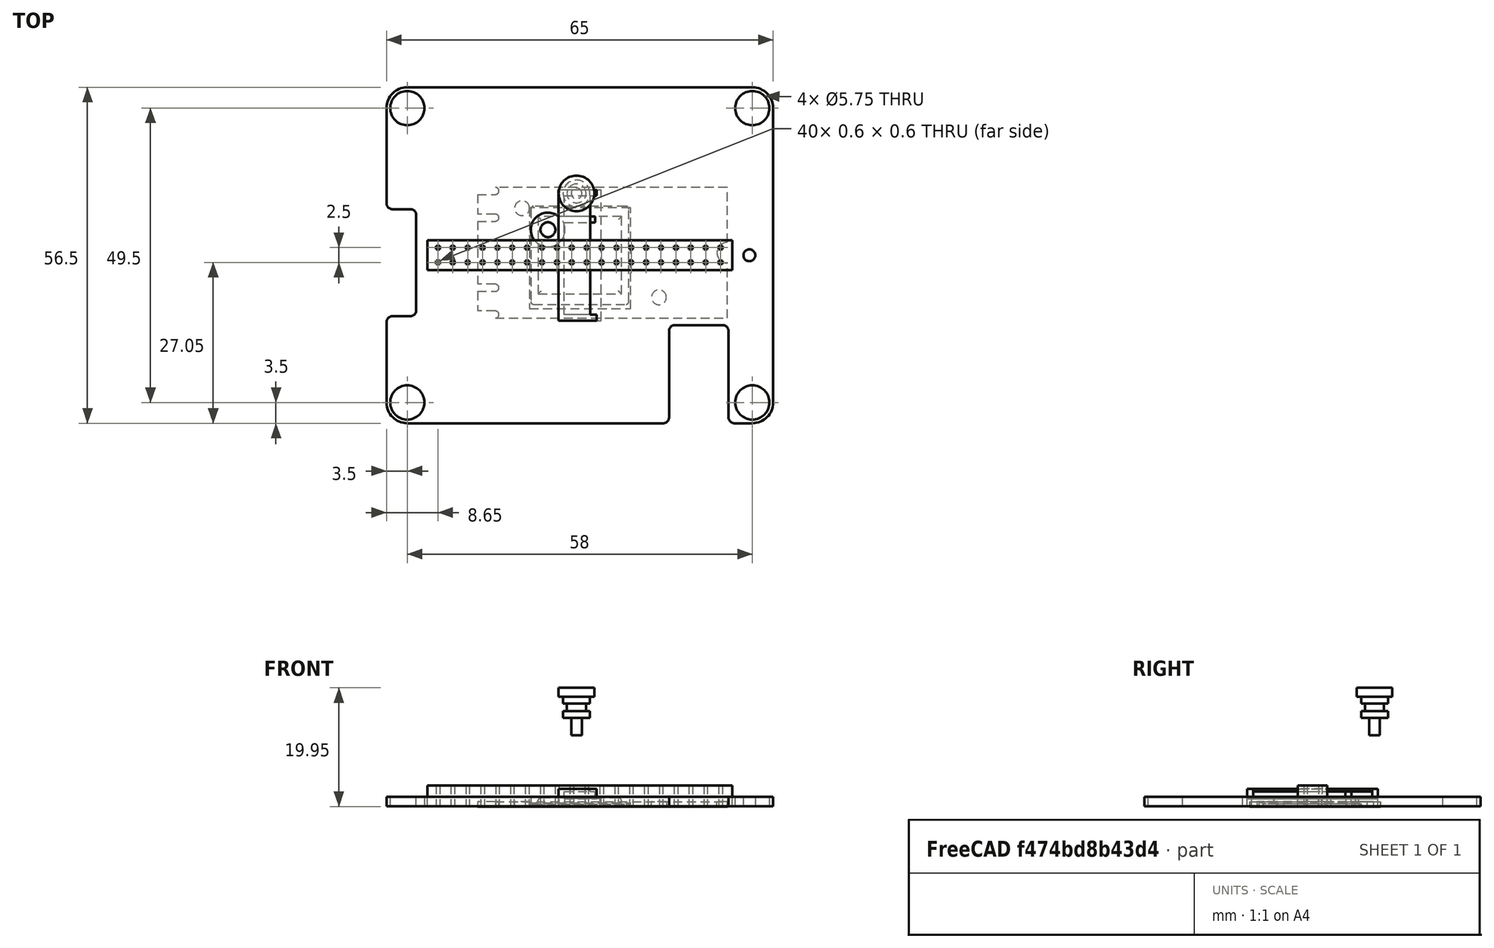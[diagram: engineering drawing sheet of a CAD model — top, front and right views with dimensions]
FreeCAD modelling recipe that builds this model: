
FCSTD DOCUMENT  (FreeCAD 1.0R39109 (Git))
Label: Raspberry Pi AI Kit
License: All rights reserved
LicenseURL: https://en.wikipedia.org/wiki/All_rights_reserved
objects: App::Link×21, Sketcher::SketchObject×14, App::FeaturePython×14, PartDesign::Pad×10, PartDesign::Body×8, PartDesign::Pocket×3, Assembly::JointGroup×3, Assembly::AssemblyObject×3, App::Part×2, Assembly::AssemblyLink×2, PartDesign::Revolution×1, PartDesign::Fillet×1
note: 81 computed .brp shape members not serialized (recipe doc carries the construction recipe); baked Part::Feature solids carry a one-line shape summary decoded from their .brp

FEATURE [Sketcher::SketchObject] Sketch
  ArcFitTolerance = 1e-06
  AttachmentSupport = -> [XY_Plane003]
  FullyConstrained = true
  MakeInternals = false
  MapMode = 5
  sketch-geometry (6):
    g0: LineSegment StartX=-21 StartY=11 StartZ=0 EndX=-21 EndY=-11 EndZ=0
    g1: LineSegment StartX=-21 StartY=-11 StartZ=0 EndX=21 EndY=-11 EndZ=0
    g2: LineSegment StartX=21 StartY=-11 StartZ=0 EndX=21 EndY=11 EndZ=0
    g3: LineSegment StartX=21 StartY=11 StartZ=0 EndX=-21 EndY=11 EndZ=0
    g4: GeomPoint X=0 Y=11 Z=0
    g5: GeomPoint X=-21 Y=0 Z=0
  constraints (14):
    c: Coincident(g0,g1)
    c: Coincident(g1,g2)
    c: Coincident(g2,g3)
    c: Coincident(g3,g0)
    c: Vertical(g0)
    c: Vertical(g2)
    c: Horizontal(g1)
    c: Horizontal(g3)
    c: DistanceY(g2,g2) = 22
    c: DistanceX(g3,g3) = 42
    c: Symmetric(g3,g3,g4)
    c: Symmetric(g0,g0,g5)
    c: Vertical(g4,g-1)
    c: Horizontal(g5,g-1)
FEATURE [PartDesign::Pad] Pad
  Direction = (0,0,1)
  Length = 0.8
  Length2 = 10
  Profile = -> Sketch
  ReferenceAxis = -> Sketch [N_Axis]
  Refine = true
  Suppressed = false
  Type = 0
FEATURE [Sketcher::SketchObject] Sketch001
  ArcFitTolerance = 1e-06
  AttachmentSupport = -> [Pad]
  ExternalGeometry = -> [Pad]
  FullyConstrained = true
  MakeInternals = false
  MapMode = 5
  Placement = pos=(0,0,0.8) rot=(0,0,1;0rad)
  sketch-geometry (27):
    g0: LineSegment StartX=-21 StartY=-9.8 StartZ=0 EndX=-21 EndY=-11 EndZ=0
    g1: LineSegment StartX=-21 StartY=-11 StartZ=0 EndX=-18 EndY=-11 EndZ=0
    g2: LineSegment StartX=-18 StartY=-11 StartZ=0 EndX=-18 EndY=-9.8 EndZ=0
    g3: LineSegment StartX=-18 StartY=-9.8 StartZ=0 EndX=-21 EndY=-9.8 EndZ=0
    g4: GeomPoint X=-18 Y=-10.4 Z=0
    g5: Circle CenterX=-18 CenterY=-10.4 CenterZ=0 NormalX=0 NormalY=0 NormalZ=1 AngleXU=0 Radius=0.6
    g6: Circle CenterX=21 CenterY=0 CenterZ=0 NormalX=0 NormalY=0 NormalZ=1 AngleXU=0 Radius=1.75
    g7: LineSegment StartX=-21 StartY=11 StartZ=0 EndX=-21 EndY=9.8 EndZ=0
    g8: LineSegment StartX=-21 StartY=9.8 StartZ=0 EndX=-18 EndY=9.8 EndZ=0
    g9: LineSegment StartX=-18 StartY=9.8 StartZ=0 EndX=-18 EndY=11 EndZ=0
    g10: LineSegment StartX=-18 StartY=11 StartZ=0 EndX=-21 EndY=11 EndZ=0
    g11: GeomPoint X=-18 Y=10.4 Z=0
    g12: Circle CenterX=-18 CenterY=10.4 CenterZ=0 NormalX=0 NormalY=0 NormalZ=1 AngleXU=0 Radius=0.6
    g13: LineSegment StartX=-21 StartY=6.5 StartZ=0 EndX=-21 EndY=5.3 EndZ=0
    g14: LineSegment StartX=-21 StartY=5.3 StartZ=0 EndX=-18 EndY=5.3 EndZ=0
    g15: LineSegment StartX=-18 StartY=5.3 StartZ=0 EndX=-18 EndY=6.5 EndZ=0
    g16: LineSegment StartX=-18 StartY=6.5 StartZ=0 EndX=-21 EndY=6.5 EndZ=0
    g17: GeomPoint X=-18 Y=5.9 Z=0
    g18: Circle CenterX=-18 CenterY=5.9 CenterZ=0 NormalX=0 NormalY=0 NormalZ=1 AngleXU=0 Radius=0.6
    g19: LineSegment StartX=-21 StartY=-5.3 StartZ=0 EndX=-21 EndY=-6.5 EndZ=0
    g20: LineSegment StartX=-21 StartY=-6.5 StartZ=0 EndX=-18 EndY=-6.5 EndZ=0
    g21: LineSegment StartX=-18 StartY=-6.5 StartZ=0 EndX=-18 EndY=-5.3 EndZ=0
    g22: LineSegment StartX=-18 StartY=-5.3 StartZ=0 EndX=-21 EndY=-5.3 EndZ=0
    g23: GeomPoint X=-18 Y=-5.9 Z=0
    g24: Circle CenterX=-18 CenterY=-5.9 CenterZ=0 NormalX=0 NormalY=0 NormalZ=1 AngleXU=0 Radius=0.6
    g25: Circle CenterX=-13.5 CenterY=7.5 CenterZ=0 NormalX=0 NormalY=0 NormalZ=1 AngleXU=0 Radius=1.25
    g26: Circle CenterX=9.5 CenterY=-7.5 CenterZ=0 NormalX=0 NormalY=0 NormalZ=1 AngleXU=0 Radius=1.25
  constraints (66):
    c: Coincident(g0,g1)
    c: Coincident(g1,g2)
    c: Coincident(g2,g3)
    c: Coincident(g3,g0)
    c: Vertical(g0)
    c: Vertical(g2)
    c: Horizontal(g1)
    c: Horizontal(g3)
    c: Symmetric(g2,g2,g4)
    c: Coincident(g5,g4)
    c: PointOnObject(g2,g5)
    c: Distance(g1,g3) = 1.2
    c: DistanceX(g3,g3) = 3
    c: Symmetric(g-6,g-6,g6)
    c: Diameter(g6) = 3.5
    c: Coincident(g7,g8)
    c: Coincident(g8,g9)
    c: Coincident(g9,g10)
    c: Coincident(g10,g7)
    c: Vertical(g7)
    c: Vertical(g9)
    c: Horizontal(g8)
    c: Horizontal(g10)
    c: Symmetric(g9,g9,g11)
    c: Coincident(g12,g11)
    c: PointOnObject(g9,g12)
    c: Distance(g8,g10) = 1.2
    c: DistanceX(g10,g10) = 3
    c: Coincident(g0,g-5)
    c: Coincident(g13,g14)
    c: Coincident(g14,g15)
    c: Coincident(g15,g16)
    c: Coincident(g16,g13)
    c: Vertical(g13)
    c: Vertical(g15)
    c: Horizontal(g14)
    c: Horizontal(g16)
    c: Symmetric(g15,g15,g17)
    c: Coincident(g18,g17)
    c: PointOnObject(g15,g18)
    c: Distance(g14,g16) = 1.2
    c: DistanceX(g16,g16) = 3
    c: Coincident(g19,g20)
    c: Coincident(g20,g21)
    c: Coincident(g21,g22)
    c: Coincident(g22,g19)
    c: Vertical(g19)
    c: Vertical(g21)
    c: Horizontal(g20)
    c: Horizontal(g22)
    c: Symmetric(g21,g21,g23)
    c: Coincident(g24,g23)
    c: PointOnObject(g21,g24)
    c: Distance(g20,g22) = 1.2
    c: DistanceX(g22,g22) = 3
    c: Coincident(g7,g-4)
    c: Distance(g-4,g16) = 4.5
    c: PointOnObject(g13,g-3)
    c: Distance(g-5,g20) = 4.5
    c: PointOnObject(g19,g-3)
    c: Diameter(g25) = 2.5
    c: Diameter(g26) = 2.5
    c: Distance(g25,g-5) = 18.5
    c: Distance(g25,g-3) = 7.5
    c: Distance(g26,g-5) = 3.5
    c: Distance(g26,g-3) = 30.5
FEATURE [PartDesign::Pocket] Pocket
  BaseFeature = -> Pad
  Direction = (0,0,-1)
  Length = 5
  Length2 = 5
  Profile = -> Sketch001
  ReferenceAxis = -> Sketch001 [N_Axis]
  Refine = true
  Suppressed = false
  Type = 0
FEATURE [PartDesign::Body] Body  label="Board"
  AllowCompound = false
  Group = -> [Sketch,Pad,Sketch001,Pocket]
  Origin = -> Origin003
  Placement = pos=(3.79899,0.428775,-0.0438795) rot=(0,0,1;0rad)
  Tip = -> Pocket
FEATURE [Sketcher::SketchObject] Sketch002
  ArcFitTolerance = 1e-06
  AttachmentSupport = -> [XZ_Plane004]
  FullyConstrained = false
  MakeInternals = false
  MapMode = 5
  Placement = pos=(0,0,0) rot=(1,0,0;1.5708rad)
  sketch-geometry (20):
    g0: LineSegment StartX=0 StartY=8.4139 StartZ=0 EndX=-0.9 EndY=8.4139 EndZ=0
    g1: LineSegment StartX=-0.9 StartY=8.4139 StartZ=0 EndX=-0.9 EndY=0.413896 EndZ=0
    g2: LineSegment StartX=-0.9 StartY=0.413896 StartZ=0 EndX=0 EndY=0.413896 EndZ=0
    g3: LineSegment StartX=0 StartY=0.413896 StartZ=0 EndX=0 EndY=8.4139 EndZ=0
    g4: LineSegment StartX=-0.9 StartY=8.4139 StartZ=0 EndX=-3 EndY=8.4139 EndZ=0
    g5: LineSegment StartX=-3 StartY=8.4139 StartZ=0 EndX=-3 EndY=6.9139 EndZ=0
    g6: LineSegment StartX=-3 StartY=6.9139 StartZ=0 EndX=-0.9 EndY=6.9139 EndZ=0
    g7: LineSegment StartX=-0.9 StartY=6.9139 StartZ=0 EndX=-0.9 EndY=8.4139 EndZ=0
    g8: LineSegment StartX=-2.25 StartY=6.9139 StartZ=0 EndX=-2.25 EndY=5.7639 EndZ=0
    g9: LineSegment StartX=-2.25 StartY=5.7639 StartZ=0 EndX=-0.9 EndY=5.7639 EndZ=0
    g10: LineSegment StartX=-0.9 StartY=5.7639 StartZ=0 EndX=-0.9 EndY=6.9139 EndZ=0
    g11: LineSegment StartX=-0.9 StartY=6.9139 StartZ=0 EndX=-2.25 EndY=6.9139 EndZ=0
    g12: LineSegment StartX=-0.9 StartY=4.5139 StartZ=0 EndX=-2.25 EndY=4.5139 EndZ=0
    g13: LineSegment StartX=-2.25 StartY=4.5139 StartZ=0 EndX=-2.25 EndY=3.3639 EndZ=0
    g14: LineSegment StartX=-2.25 StartY=3.3639 StartZ=0 EndX=-0.9 EndY=3.3639 EndZ=0
    g15: LineSegment StartX=-0.9 StartY=3.3639 StartZ=0 EndX=-0.9 EndY=4.5139 EndZ=0
    g16: LineSegment StartX=-1.6 StartY=5.7639 StartZ=0 EndX=-1.6 EndY=4.5139 EndZ=0
    g17: LineSegment StartX=-1.6 StartY=4.5139 StartZ=0 EndX=-0.9 EndY=4.5139 EndZ=0
    g18: LineSegment StartX=-0.9 StartY=4.5139 StartZ=0 EndX=-0.9 EndY=5.7639 EndZ=0
    g19: LineSegment StartX=-0.9 StartY=5.7639 StartZ=0 EndX=-1.6 EndY=5.7639 EndZ=0
  constraints (57):
    c: Coincident(g0,g1)
    c: Coincident(g1,g2)
    c: Coincident(g2,g3)
    c: Coincident(g3,g0)
    c: Horizontal(g0)
    c: Horizontal(g2)
    c: Vertical(g1)
    c: Vertical(g3)
    c: PointOnObject(g0,g-2)
    c: DistanceX(g0,g0) = 0.9
    c: Coincident(g4,g5)
    c: Coincident(g5,g6)
    c: Coincident(g6,g7)
    c: Coincident(g7,g4)
    c: Horizontal(g4)
    c: Horizontal(g6)
    c: Vertical(g5)
    c: Vertical(g7)
    c: Coincident(g4,g0)
    c: DistanceY(g3,g3) = 8
    c: Distance(g6,g4) = 1.5
    c: DistanceX(g4,g0) = 3
    c: Coincident(g8,g9)
    c: Coincident(g9,g10)
    c: Coincident(g10,g11)
    c: Coincident(g11,g8)
    c: Vertical(g8)
    c: Vertical(g10)
    c: Horizontal(g9)
    c: Horizontal(g11)
    c: PointOnObject(g8,g6)
    c: PointOnObject(g9,g1)
    c: Distance(g8,g3) = 2.25
    c: DistanceY(g8,g8) = 1.15
    c: Coincident(g12,g13)
    c: Coincident(g13,g14)
    c: Coincident(g14,g15)
    c: Coincident(g15,g12)
    c: Horizontal(g12)
    c: Horizontal(g14)
    c: Vertical(g13)
    c: Vertical(g15)
    c: PointOnObject(g12,g1)
    c: DistanceY(g13,g13) = 1.15
    c: Distance(g12,g9) = 1.25
    c: Vertical(g8,g12)
    c: Coincident(g16,g17)
    c: Coincident(g17,g18)
    c: Coincident(g18,g19)
    c: Coincident(g19,g16)
    c: Vertical(g16)
    c: Vertical(g18)
    c: Horizontal(g17)
    c: Horizontal(g19)
    c: PointOnObject(g16,g9)
    c: Coincident(g17,g12)
    c: Distance(g3,g16) = 1.6
FEATURE [PartDesign::Revolution] Revolution
  Angle = 360
  Angle2 = 60
  Axis = (0,2e-16,1)
  Base = (0,0,0)
  Placement = pos=(0,0,0) rot=(1,0,0;1.5708rad)
  Profile = -> Sketch002
  ReferenceAxis = -> Sketch002 [V_Axis]
  Refine = true
  Suppressed = false
  Type = 0
FEATURE [PartDesign::Body] Body001  label="Pin"
  AllowCompound = false
  Group = -> [Sketch002,Revolution]
  Origin = -> Origin004
  Placement = pos=(-0.558638,10.4085,11.496) rot=(0,0,1;0rad)
  Tip = -> Revolution
FEATURE [Sketcher::SketchObject] Sketch003
  ArcFitTolerance = 1e-06
  AttachmentSupport = -> [XY_Plane007]
  FullyConstrained = false
  MakeInternals = false
  MapMode = 5
  sketch-geometry (4):
    g0: LineSegment StartX=-8.47777 StartY=8.01213 StartZ=0 EndX=-8.47777 EndY=-8.98787 EndZ=0
    g1: LineSegment StartX=-8.47777 StartY=-8.98787 StartZ=0 EndX=8.52223 EndY=-8.98787 EndZ=0
    g2: LineSegment StartX=8.52223 StartY=-8.98787 StartZ=0 EndX=8.52223 EndY=8.01213 EndZ=0
    g3: LineSegment StartX=8.52223 StartY=8.01213 StartZ=0 EndX=-8.47777 EndY=8.01213 EndZ=0
  constraints (10):
    c: Coincident(g0,g1)
    c: Coincident(g1,g2)
    c: Coincident(g2,g3)
    c: Coincident(g3,g0)
    c: Vertical(g0)
    c: Vertical(g2)
    c: Horizontal(g1)
    c: Horizontal(g3)
    c: DistanceX(g3,g3) = 17
    c: DistanceY(g2,g2) = 17
FEATURE [PartDesign::Pad] Pad001
  Direction = (0,0,1)
  Length = 0.6
  Length2 = 10
  Profile = -> Sketch003
  ReferenceAxis = -> Sketch003 [N_Axis]
  Refine = true
  Suppressed = false
  Type = 0
FEATURE [PartDesign::Body] Body002  label="Chip Platform"
  AllowCompound = false
  Group = -> [Sketch003,Pad001]
  Origin = -> Origin007
  Tip = -> Pad001
FEATURE [Sketcher::SketchObject] Sketch004
  ArcFitTolerance = 1e-06
  AttachmentSupport = -> [XY_Plane008]
  FullyConstrained = true
  MakeInternals = false
  MapMode = 5
  sketch-geometry (14):
    g0: LineSegment StartX=-8.25 StartY=7.75 StartZ=0 EndX=-8.25 EndY=-7.75 EndZ=0
    g1: LineSegment StartX=-7.75 StartY=-8.25 StartZ=0 EndX=7.75 EndY=-8.25 EndZ=0
    g2: LineSegment StartX=8.25 StartY=-7.75 StartZ=0 EndX=8.25 EndY=7.75 EndZ=0
    g3: LineSegment StartX=7.75 StartY=8.25 StartZ=0 EndX=-7.75 EndY=8.25 EndZ=0
    g4: GeomPoint X=8.25 Y=0 Z=0
    g5: GeomPoint X=0 Y=8.25 Z=0
    g6: ArcOfCircle CenterX=7.75 CenterY=7.75 CenterZ=0 NormalX=0 NormalY=0 NormalZ=1 AngleXU=0 Radius=0.5 StartAngle=2e-16 EndAngle=1.5708
    g7: GeomPoint [constr] X=8.25 Y=8.25 Z=0
    g8: ArcOfCircle CenterX=-7.75 CenterY=7.75 CenterZ=0 NormalX=0 NormalY=0 NormalZ=1 AngleXU=0 Radius=0.5 StartAngle=1.5708 EndAngle=3.14159
    g9: GeomPoint [constr] X=-8.25 Y=8.25 Z=0
    g10: ArcOfCircle CenterX=-7.75 CenterY=-7.75 CenterZ=0 NormalX=0 NormalY=0 NormalZ=1 AngleXU=0 Radius=0.5 StartAngle=3.14159 EndAngle=4.71239
    g11: GeomPoint [constr] X=-8.25 Y=-8.25 Z=0
    g12: ArcOfCircle CenterX=7.75 CenterY=-7.75 CenterZ=0 NormalX=0 NormalY=0 NormalZ=1 AngleXU=0 Radius=0.5 StartAngle=4.71239 EndAngle=6.28319
    g13: GeomPoint [constr] X=8.25 Y=-8.25 Z=0
  constraints (30):
    c: Vertical(g0)
    c: Vertical(g2)
    c: Horizontal(g1)
    c: Horizontal(g3)
    c: DistanceX(g9,g7) = 16.5
    c: DistanceY(g13,g7) = 16.5
    c: Symmetric(g13,g7,g4)
    c: Symmetric(g7,g9,g5)
    c: Vertical(g5,g-1)
    c: Horizontal(g4,g-1)
    c: PointOnObject(g7,g2)
    c: PointOnObject(g7,g3)
    c: Tangent(g2,g6) = -1.5708
    c: Tangent(g3,g6) = -1.5708
    c: PointOnObject(g9,g0)
    c: PointOnObject(g9,g3)
    c: Tangent(g0,g8) = -1.5708
    c: Tangent(g3,g8) = -1.5708
    c: PointOnObject(g11,g0)
    c: PointOnObject(g11,g1)
    c: Tangent(g0,g10) = -1.5708
    c: Tangent(g1,g10) = -1.5708
    c: PointOnObject(g13,g1)
    c: PointOnObject(g13,g2)
    c: Tangent(g1,g12) = -1.5708
    c: Tangent(g2,g12) = -1.5708
    c: Radius(g8) = 0.5
    c: Radius(g6) = 0.5
    c: Radius(g12) = 0.5
    c: Radius(g10) = 0.5
FEATURE [PartDesign::Pad] Pad002
  Direction = (0,0,1)
  Length = 0.4
  Length2 = 10
  Profile = -> Sketch004
  ReferenceAxis = -> Sketch004 [N_Axis]
  Refine = true
  Suppressed = false
  Type = 0
FEATURE [Sketcher::SketchObject] Sketch005
  ArcFitTolerance = 1e-06
  AttachmentSupport = -> [Pad002]
  FullyConstrained = true
  MakeInternals = false
  MapMode = 5
  Placement = pos=(0,0,0.4) rot=(0,0,1;0rad)
  sketch-geometry (6):
    g0: LineSegment StartX=-7 StartY=6.5 StartZ=0 EndX=-7 EndY=-6.5 EndZ=0
    g1: LineSegment StartX=-7 StartY=-6.5 StartZ=0 EndX=7 EndY=-6.5 EndZ=0
    g2: LineSegment StartX=7 StartY=-6.5 StartZ=0 EndX=7 EndY=6.5 EndZ=0
    g3: LineSegment StartX=7 StartY=6.5 StartZ=0 EndX=-7 EndY=6.5 EndZ=0
    g4: GeomPoint X=0 Y=6.5 Z=0
    g5: GeomPoint X=7 Y=-1e-16 Z=0
  constraints (14):
    c: Coincident(g0,g1)
    c: Coincident(g1,g2)
    c: Coincident(g2,g3)
    c: Coincident(g3,g0)
    c: Vertical(g0)
    c: Vertical(g2)
    c: Horizontal(g1)
    c: Horizontal(g3)
    c: Symmetric(g3,g3,g4)
    c: Symmetric(g2,g2,g5)
    c: Vertical(g4,g-1)
    c: Horizontal(g5,g-1)
    c: DistanceX(g3,g3) = 14
    c: DistanceY(g2,g2) = 13
FEATURE [PartDesign::Pad] Pad003
  BaseFeature = -> Pad002
  Direction = (0,0,1)
  Length = 1
  Length2 = 10
  Profile = -> Sketch005
  ReferenceAxis = -> Sketch005 [N_Axis]
  Refine = true
  Suppressed = false
  Type = 0
FEATURE [PartDesign::Fillet] Fillet
  Base = -> Pad003 [Face15]
  BaseFeature = -> Pad003
  Radius = 0.5
  Refine = true
  SupportTransform = false
  Suppressed = false
  UseAllEdges = false
FEATURE [PartDesign::Body] Body003  label="Chip"
  AllowCompound = false
  Group = -> [Sketch004,Pad002,Sketch005,Pad003,Fillet]
  Origin = -> Origin008
  Tip = -> Fillet
FEATURE [App::Part] Part  label="Hailo AI Module"
  Group = -> [Body,Body002,Body003]
  Origin = -> Origin005
  Placement = pos=(-4.7276,-1.1891,7.43734) rot=(0,0,1;0rad)
FEATURE [App::Link] Board  label="Board001"
  LinkedObject = -> Body
FEATURE [App::FeaturePython] GroundedJoint  # Assembly grounded joint (typed FeaturePython)
  ObjectToGround = -> Board
FEATURE [App::Link] Chip_Platform  label="Chip Platform001"
  LinkPlacement = pos=(-2.02223,0.487867,0.8) rot=(0,0,1;0rad)
  LinkedObject = -> Body002
  Placement = pos=(-2.02223,0.487867,0.8) rot=(0,0,1;0rad)
FEATURE [App::Link] Chip  label="Chip001"
  LinkPlacement = pos=(-2,1.8e-15,1.4) rot=(0,0,1;0rad)
  LinkedObject = -> Body003
  Placement = pos=(-2,1.8e-15,1.4) rot=(0,0,1;0rad)
FEATURE [App::FeaturePython] Joint  label="Fixed"  # Assembly joint (typed FeaturePython)
  Activated = true
  AngleMax = 0
  AngleMin = 0
  Detach1 = false
  Detach2 = false
  Distance = 0
  Distance2 = 0
  EnableAngleMax = false
  EnableAngleMin = false
  EnableLengthMax = false
  EnableLengthMin = false
  JointType = 0 (Fixed)
  LengthMax = 0
  LengthMin = 0
  Offset2 = pos=(0,-2.5,-3.5) rot=(0,0,1;0rad)
  Placement1 = pos=(0.0222293,-8.98787,0) rot=(0.707107,0,0.707107;3.14159rad)
  Placement2 = pos=(-2,-8.5,0.8) rot=(0.707107,0,0.707107;3.14159rad)
  Reference1 = -> Assembly [Chip_Platform.Edge6,Chip_Platform.Edge6]
  Reference2 = -> Assembly [Board.Edge37,Board.Edge37]
FEATURE [App::FeaturePython] Joint001  label="Fixed001"  # Assembly joint (typed FeaturePython)
  Activated = true
  AngleMax = 0
  AngleMin = 0
  Detach1 = false
  Detach2 = false
  Distance = 0
  Distance2 = 0
  EnableAngleMax = false
  EnableAngleMin = false
  EnableLengthMax = false
  EnableLengthMin = false
  JointType = 0 (Fixed)
  LengthMax = 0
  LengthMin = 0
  Offset2 = pos=(0,-0.25,0) rot=(0,0,1;0rad)
  Placement1 = pos=(0,-8.25,0) rot=(0.707107,0,0.707107;3.14159rad)
  Placement2 = pos=(0.0222293,-8.73787,0.6) rot=(0.707107,0,0.707107;3.14159rad)
  Reference1 = -> Assembly [Chip.Edge39,Chip.Edge39]
  Reference2 = -> Assembly [Chip_Platform.Edge7,Chip_Platform.Edge7]
FEATURE [Assembly::JointGroup] Joints
  Group = -> [GroundedJoint,Joint,Joint001]
FEATURE [Assembly::AssemblyObject] Assembly  label="Hailo AI Module Assembly"
  Group = -> [Joints,Board,GroundedJoint,Chip_Platform,Chip,Joint,Joint001]
  Origin = -> Origin
  Type = Assembly
FEATURE [Sketcher::SketchObject] Sketch006
  ArcFitTolerance = 1e-06
  AttachmentSupport = -> [XY_Plane010]
  FullyConstrained = true
  MakeInternals = false
  MapMode = 5
  sketch-geometry (38):
    g0: LineSegment StartX=-29 StartY=28.25 StartZ=0 EndX=29 EndY=28.25 EndZ=0
    g1: LineSegment StartX=32.5 StartY=24.75 StartZ=0 EndX=32.5 EndY=-24.75 EndZ=0
    g2: LineSegment StartX=29 StartY=-28.25 StartZ=0 EndX=26 EndY=-28.25 EndZ=0
    g3: LineSegment StartX=25 StartY=-27.25 StartZ=0 EndX=25 EndY=-12.75 EndZ=0
    g4: LineSegment StartX=24 StartY=-11.75 StartZ=0 EndX=16 EndY=-11.75 EndZ=0
    g5: LineSegment StartX=15 StartY=-12.75 StartZ=0 EndX=15 EndY=-27.25 EndZ=0
    g6: LineSegment StartX=14 StartY=-28.25 StartZ=0 EndX=-29 EndY=-28.25 EndZ=0
    g7: GeomPoint X=0 Y=28.25 Z=0
    g8: LineSegment StartX=-32.5 StartY=-24.75 StartZ=0 EndX=-32.5 EndY=-11.25 EndZ=0
    g9: LineSegment StartX=-31.5 StartY=-10.25 StartZ=0 EndX=-28.5 EndY=-10.25 EndZ=0
    g10: LineSegment StartX=-27.5 StartY=-9.25 StartZ=0 EndX=-27.5 EndY=6.75 EndZ=0
    g11: LineSegment StartX=-28.5 StartY=7.75 StartZ=0 EndX=-31.5 EndY=7.75 EndZ=0
    g12: LineSegment StartX=-32.5 StartY=8.75 StartZ=0 EndX=-32.5 EndY=24.75 EndZ=0
    g13: GeomPoint X=32.5 Y=0 Z=0
    g14: ArcOfCircle CenterX=29 CenterY=24.75 CenterZ=0 NormalX=0 NormalY=0 NormalZ=1 AngleXU=0 Radius=3.5 StartAngle=0 EndAngle=1.5708
    g15: GeomPoint [constr] X=32.5 Y=28.25 Z=0
    g16: ArcOfCircle CenterX=-29 CenterY=24.75 CenterZ=0 NormalX=0 NormalY=0 NormalZ=1 AngleXU=0 Radius=3.5 StartAngle=1.5708 EndAngle=3.14159
    g17: GeomPoint [constr] X=-32.5 Y=28.25 Z=0
    g18: ArcOfCircle CenterX=-29 CenterY=-24.75 CenterZ=0 NormalX=0 NormalY=0 NormalZ=1 AngleXU=0 Radius=3.5 StartAngle=3.14159 EndAngle=4.71239
    g19: GeomPoint [constr] X=-32.5 Y=-28.25 Z=0
    g20: ArcOfCircle CenterX=29 CenterY=-24.75 CenterZ=0 NormalX=0 NormalY=0 NormalZ=1 AngleXU=0 Radius=3.5 StartAngle=4.71239 EndAngle=6.28319
    g21: GeomPoint [constr] X=32.5 Y=-28.25 Z=0
    g22: ArcOfCircle CenterX=-31.5 CenterY=8.75 CenterZ=0 NormalX=0 NormalY=0 NormalZ=1 AngleXU=0 Radius=1 StartAngle=3.14159 EndAngle=4.71239
    g23: GeomPoint [constr] X=-32.5 Y=7.75 Z=0
    g24: ArcOfCircle CenterX=-28.5 CenterY=6.75 CenterZ=0 NormalX=0 NormalY=0 NormalZ=1 AngleXU=0 Radius=1 StartAngle=0 EndAngle=1.5708
    g25: GeomPoint [constr] X=-27.5 Y=7.75 Z=0
    g26: ArcOfCircle CenterX=-28.5 CenterY=-9.25 CenterZ=0 NormalX=0 NormalY=0 NormalZ=1 AngleXU=0 Radius=1 StartAngle=4.71239 EndAngle=6.28319
    g27: GeomPoint [constr] X=-27.5 Y=-10.25 Z=0
    g28: ArcOfCircle CenterX=-31.5 CenterY=-11.25 CenterZ=0 NormalX=0 NormalY=0 NormalZ=1 AngleXU=0 Radius=1 StartAngle=1.5708 EndAngle=3.14159
    g29: GeomPoint [constr] X=-32.5 Y=-10.25 Z=0
    g30: ArcOfCircle CenterX=14 CenterY=-27.25 CenterZ=0 NormalX=0 NormalY=0 NormalZ=1 AngleXU=0 Radius=1 StartAngle=4.71239 EndAngle=6.28319
    g31: GeomPoint [constr] X=15 Y=-28.25 Z=0
    g32: ArcOfCircle CenterX=16 CenterY=-12.75 CenterZ=0 NormalX=0 NormalY=0 NormalZ=1 AngleXU=0 Radius=1 StartAngle=1.5708 EndAngle=3.14159
    g33: GeomPoint [constr] X=15 Y=-11.75 Z=0
    g34: ArcOfCircle CenterX=24 CenterY=-12.75 CenterZ=0 NormalX=0 NormalY=0 NormalZ=1 AngleXU=0 Radius=1 StartAngle=4e-16 EndAngle=1.5708
    g35: GeomPoint [constr] X=25 Y=-11.75 Z=0
    g36: ArcOfCircle CenterX=26 CenterY=-27.25 CenterZ=0 NormalX=0 NormalY=0 NormalZ=1 AngleXU=0 Radius=1 StartAngle=3.14159 EndAngle=4.71239
    g37: GeomPoint [constr] X=25 Y=-28.25 Z=0
  constraints (86):
    c: Horizontal(g0)
    c: Vertical(g1)
    c: Horizontal(g2)
    c: Vertical(g3)
    c: Horizontal(g4)
    c: Vertical(g5)
    c: Horizontal(g6)
    c: DistanceX(g17,g15) = 65
    c: Symmetric(g17,g15,g7)
    c: Vertical(g7,g-1)
    c: Horizontal(g37,g31)
    c: DistanceX(g37,g21) = 7.5
    c: DistanceX(g33,g35) = 10
    c: DistanceY(g37,g35) = 16.5
    c: Vertical(g8)
    c: Horizontal(g9)
    c: Vertical(g10)
    c: Horizontal(g11)
    c: Vertical(g12)
    c: Vertical(g23,g29)
    c: Symmetric(g15,g21,g13)
    c: Horizontal(g13,g-1)
    c: DistanceY(g21,g15) = 56.5
    c: DistanceX(g23,g25) = 5
    c: DistanceY(g27,g25) = 18
    c: DistanceY(g19,g29) = 18
    c: PointOnObject(g15,g0)
    c: PointOnObject(g15,g1)
    c: Tangent(g0,g14) = 1.5708
    c: Tangent(g1,g14) = 1.5708
    c: PointOnObject(g17,g0)
    c: PointOnObject(g17,g12)
    c: Tangent(g0,g16) = 1.5708
    c: Tangent(g12,g16) = 1.5708
    c: PointOnObject(g19,g6)
    c: PointOnObject(g19,g8)
    c: Tangent(g6,g18) = 1.5708
    c: Tangent(g8,g18) = 1.5708
    c: PointOnObject(g21,g1)
    c: PointOnObject(g21,g2)
    c: Tangent(g1,g20) = 1.5708
    c: Tangent(g2,g20) = 1.5708
    c: Radius(g20) = 3.5
    c: Radius(g14) = 3.5
    c: Radius(g16) = 3.5
    c: Radius(g18) = 3.5
    c: PointOnObject(g23,g11)
    c: PointOnObject(g23,g12)
    c: Tangent(g11,g22) = 1.5708
    c: Tangent(g12,g22) = 1.5708
    c: PointOnObject(g25,g10)
    c: PointOnObject(g25,g11)
    c: Tangent(g10,g24) = -1.5708
    c: Tangent(g11,g24) = -1.5708
    c: PointOnObject(g27,g9)
    c: PointOnObject(g27,g10)
    c: Tangent(g9,g26) = -1.5708
    c: Tangent(g10,g26) = -1.5708
    c: PointOnObject(g29,g8)
    c: PointOnObject(g29,g9)
    c: Tangent(g8,g28) = 1.5708
    c: Tangent(g9,g28) = 1.5708
    c: PointOnObject(g31,g5)
    c: PointOnObject(g31,g6)
    c: Tangent(g5,g30) = 1.5708
    c: Tangent(g6,g30) = 1.5708
    c: PointOnObject(g33,g4)
    c: PointOnObject(g33,g5)
    c: Tangent(g4,g32) = -1.5708
    c: Tangent(g5,g32) = -1.5708
    c: PointOnObject(g35,g3)
    c: PointOnObject(g35,g4)
    c: Tangent(g3,g34) = -1.5708
    c: Tangent(g4,g34) = -1.5708
    c: PointOnObject(g37,g2)
    c: PointOnObject(g37,g3)
    c: Tangent(g2,g36) = 1.5708
    c: Tangent(g3,g36) = 1.5708
    c: Radius(g22) = 1
    c: Radius(g24) = 1
    c: Radius(g26) = 1
    c: Radius(g28) = 1
    c: Radius(g30) = 1
    c: Radius(g32) = 1
    c: Radius(g34) = 1
    c: Radius(g36) = 1
FEATURE [PartDesign::Pad] Pad004
  Direction = (0,0,1)
  Length = 1.57
  Length2 = 10
  Profile = -> Sketch006
  ReferenceAxis = -> Sketch006 [N_Axis]
  Refine = true
  Suppressed = false
  Type = 0
FEATURE [Sketcher::SketchObject] Sketch007
  ArcFitTolerance = 1e-06
  AttachmentSupport = -> [Pad004]
  ExternalGeometry = -> [Pad004]
  FullyConstrained = true
  MakeInternals = false
  MapMode = 5
  Placement = pos=(0,0,1.57) rot=(0,0,1;0rad)
  sketch-geometry (5):
    g0: Circle CenterX=-29 CenterY=-24.75 CenterZ=0 NormalX=0 NormalY=0 NormalZ=1 AngleXU=0 Radius=2.875
    g1: Circle CenterX=-29 CenterY=24.75 CenterZ=0 NormalX=0 NormalY=0 NormalZ=1 AngleXU=0 Radius=2.875
    g2: Circle CenterX=29 CenterY=24.75 CenterZ=0 NormalX=0 NormalY=0 NormalZ=1 AngleXU=0 Radius=2.875
    g3: Circle CenterX=29 CenterY=-24.75 CenterZ=0 NormalX=0 NormalY=0 NormalZ=1 AngleXU=0 Radius=2.875
    g4: Circle CenterX=28.5 CenterY=0 CenterZ=0 NormalX=0 NormalY=0 NormalZ=1 AngleXU=0 Radius=1
  constraints (15):
    c: Distance(g0,g-3) = 3.5
    c: Distance(g0,g-7) = 3.5
    c: Diameter(g0) = 5.75
    c: Diameter(g1) = 5.75
    c: Diameter(g2) = 5.75
    c: Diameter(g3) = 5.75
    c: Distance(g1,g-6) = 3.5
    c: Distance(g1,g-5) = 3.5
    c: Distance(g2,g-5) = 3.5
    c: Distance(g2,g-4) = 3.5
    c: Distance(g3,g-4) = 3.5
    c: Distance(g3,g-3) = 3.5
    c: PointOnObject(g4,g-1)
    c: Diameter(g4) = 2
    c: Distance(g4,g-4) = 4
FEATURE [PartDesign::Pocket] Pocket001
  BaseFeature = -> Pad004
  Direction = (0,0,-1)
  Length = 5
  Length2 = 5
  Profile = -> Sketch007
  ReferenceAxis = -> Sketch007 [N_Axis]
  Refine = true
  Suppressed = false
  Type = 0
FEATURE [PartDesign::Body] Body004  label="Board002"
  AllowCompound = false
  Group = -> [Sketch006,Pad004,Sketch007,Pocket001]
  Origin = -> Origin010
  Tip = -> Pocket001
FEATURE [Sketcher::SketchObject] Sketch008
  ArcFitTolerance = 1e-06
  AttachmentSupport = -> [XY_Plane011]
  FullyConstrained = false
  MakeInternals = false
  MapMode = 5
  sketch-geometry (2):
    g0: Circle CenterX=-5.35776 CenterY=4.30507 CenterZ=0 NormalX=0 NormalY=0 NormalZ=1 AngleXU=0 Radius=2.875
    g1: Circle CenterX=-5.35776 CenterY=4.30507 CenterZ=0 NormalX=0 NormalY=0 NormalZ=1 AngleXU=0 Radius=1.25
  constraints (3):
    c: Diameter(g0) = 5.75
    c: Coincident(g1,g0)
    c: Diameter(g1) = 2.5
FEATURE [Sketcher::SketchObject] Sketch009
  ArcFitTolerance = 1e-06
  AttachmentSupport = -> [XY_Plane012]
  FullyConstrained = true
  MakeInternals = false
  MapMode = 5
  sketch-geometry (6):
    g0: LineSegment StartX=-3.6 StartY=11 StartZ=0 EndX=-3.6 EndY=-11 EndZ=0
    g1: LineSegment StartX=-3.6 StartY=-11 StartZ=0 EndX=3.6 EndY=-11 EndZ=0
    g2: LineSegment StartX=3.6 StartY=-11 StartZ=0 EndX=3.6 EndY=11 EndZ=0
    g3: LineSegment StartX=3.6 StartY=11 StartZ=0 EndX=-3.6 EndY=11 EndZ=0
    g4: GeomPoint X=0 Y=11 Z=0
    g5: GeomPoint X=3.6 Y=0 Z=0
  constraints (14):
    c: Coincident(g0,g1)
    c: Coincident(g1,g2)
    c: Coincident(g2,g3)
    c: Coincident(g3,g0)
    c: Vertical(g0)
    c: Vertical(g2)
    c: Horizontal(g1)
    c: Horizontal(g3)
    c: Symmetric(g3,g3,g4)
    c: Symmetric(g2,g2,g5)
    c: Vertical(g4,g-1)
    c: Horizontal(g5,g-1)
    c: DistanceY(g2,g2) = 22
    c: DistanceX(g3,g3) = 7.2
FEATURE [PartDesign::Pad] Pad006
  Direction = (0,0,1)
  Length = 1.25
  Length2 = 10
  Profile = -> Sketch009
  ReferenceAxis = -> Sketch009 [N_Axis]
  Refine = true
  Suppressed = false
  Type = 0
FEATURE [Sketcher::SketchObject] Sketch010
  ArcFitTolerance = 1e-06
  AttachmentSupport = -> [Pad006]
  ExternalGeometry = -> [Pad006]
  FullyConstrained = true
  MakeInternals = false
  MapMode = 5
  Placement = pos=(0,0,1.25) rot=(0,0,1;0rad)
  sketch-geometry (16):
    g0: LineSegment StartX=-3.6 StartY=11 StartZ=0 EndX=-3.6 EndY=-11 EndZ=0
    g1: LineSegment StartX=-3.6 StartY=-11 StartZ=0 EndX=-2.6 EndY=-11 EndZ=0
    g2: LineSegment StartX=-2.6 StartY=-11 StartZ=0 EndX=-2.6 EndY=11 EndZ=0
    g3: LineSegment StartX=-2.6 StartY=11 StartZ=0 EndX=-3.6 EndY=11 EndZ=0
    g4: LineSegment StartX=-2.6 StartY=11 StartZ=0 EndX=-2.6 EndY=10 EndZ=0
    g5: LineSegment StartX=-2.6 StartY=10 StartZ=0 EndX=2.85 EndY=10 EndZ=0
    g6: LineSegment StartX=2.85 StartY=10 StartZ=0 EndX=2.85 EndY=11 EndZ=0
    g7: LineSegment StartX=2.85 StartY=11 StartZ=0 EndX=-2.6 EndY=11 EndZ=0
    g8: LineSegment StartX=-2.6 StartY=6.5 StartZ=0 EndX=-2.6 EndY=5.5 EndZ=0
    g9: LineSegment StartX=-2.6 StartY=5.5 StartZ=0 EndX=2.6 EndY=5.5 EndZ=0
    g10: LineSegment StartX=2.6 StartY=5.5 StartZ=0 EndX=2.6 EndY=6.5 EndZ=0
    g11: LineSegment StartX=2.6 StartY=6.5 StartZ=0 EndX=-2.6 EndY=6.5 EndZ=0
    g12: LineSegment StartX=-2.6 StartY=-11 StartZ=0 EndX=2.85 EndY=-11 EndZ=0
    g13: LineSegment StartX=2.85 StartY=-11 StartZ=0 EndX=2.85 EndY=-10 EndZ=0
    g14: LineSegment StartX=2.85 StartY=-10 StartZ=0 EndX=-2.6 EndY=-10 EndZ=0
    g15: LineSegment StartX=-2.6 StartY=-10 StartZ=0 EndX=-2.6 EndY=-11 EndZ=0
  constraints (45):
    c: Coincident(g0,g1)
    c: Coincident(g1,g2)
    c: Coincident(g2,g3)
    c: Coincident(g3,g0)
    c: Vertical(g0)
    c: Vertical(g2)
    c: Horizontal(g1)
    c: Horizontal(g3)
    c: Coincident(g0,g-6)
    c: PointOnObject(g1,g-5)
    c: Coincident(g4,g5)
    c: Coincident(g5,g6)
    c: Coincident(g6,g7)
    c: Coincident(g7,g4)
    c: Vertical(g4)
    c: Vertical(g6)
    c: Horizontal(g5)
    c: Horizontal(g7)
    c: Coincident(g4,g2)
    c: Coincident(g8,g9)
    c: Coincident(g9,g10)
    c: Coincident(g10,g11)
    c: Coincident(g11,g8)
    c: Vertical(g8)
    c: Vertical(g10)
    c: Horizontal(g9)
    c: Horizontal(g11)
    c: PointOnObject(g8,g2)
    c: Coincident(g12,g13)
    c: Coincident(g13,g14)
    c: Coincident(g14,g15)
    c: Coincident(g15,g12)
    c: Horizontal(g12)
    c: Horizontal(g14)
    c: Vertical(g13)
    c: Vertical(g15)
    c: Coincident(g12,g1)
    c: Distance(g-4,g13) = 0.75
    c: Distance(g-4,g6) = 0.75
    c: Distance(g-4,g10) = 1
    c: DistanceY(g10,g10) = 1
    c: DistanceY(g6,g6) = 1
    c: DistanceY(g13,g13) = 1
    c: DistanceX(g3,g3) = 1
    c: Distance(g7,g11) = 4.5
FEATURE [PartDesign::Pad] Pad007
  BaseFeature = -> Pad006
  Direction = (0,0,1)
  Length = 1.2
  Length2 = 10
  Profile = -> Sketch010
  ReferenceAxis = -> Sketch010 [N_Axis]
  Refine = true
  Suppressed = false
  Type = 0
FEATURE [Sketcher::SketchObject] Sketch011
  ArcFitTolerance = 1e-06
  AttachmentSupport = -> [Pad007]
  ExternalGeometry = -> [Pad007]
  FullyConstrained = true
  MakeInternals = false
  MapMode = 5
  Placement = pos=(0,0,2.45) rot=(0,0,1;0rad)
  sketch-geometry (12):
    g0: LineSegment StartX=-3.6 StartY=11 StartZ=0 EndX=-3.6 EndY=-11 EndZ=0
    g1: LineSegment StartX=-3.6 StartY=-11 StartZ=0 EndX=1.75 EndY=-11 EndZ=0
    g2: LineSegment StartX=1.75 StartY=-11 StartZ=0 EndX=1.75 EndY=11 EndZ=0
    g3: LineSegment StartX=1.75 StartY=11 StartZ=0 EndX=-3.6 EndY=11 EndZ=0
    g4: LineSegment StartX=1.75 StartY=-11 StartZ=0 EndX=2.85 EndY=-11 EndZ=0
    g5: LineSegment StartX=2.85 StartY=-11 StartZ=0 EndX=2.85 EndY=-10 EndZ=0
    g6: LineSegment StartX=2.85 StartY=-10 StartZ=0 EndX=1.75 EndY=-10 EndZ=0
    g7: LineSegment StartX=1.75 StartY=-10 StartZ=0 EndX=1.75 EndY=-11 EndZ=0
    g8: LineSegment StartX=1.75 StartY=11 StartZ=0 EndX=1.75 EndY=10 EndZ=0
    g9: LineSegment StartX=1.75 StartY=10 StartZ=0 EndX=2.85 EndY=10 EndZ=0
    g10: LineSegment StartX=2.85 StartY=10 StartZ=0 EndX=2.85 EndY=11 EndZ=0
    g11: LineSegment StartX=2.85 StartY=11 StartZ=0 EndX=1.75 EndY=11 EndZ=0
  constraints (31):
    c: Coincident(g0,g1)
    c: Coincident(g1,g2)
    c: Coincident(g2,g3)
    c: Coincident(g3,g0)
    c: Vertical(g0)
    c: Vertical(g2)
    c: Horizontal(g1)
    c: Horizontal(g3)
    c: Coincident(g0,g-4)
    c: PointOnObject(g1,g-5)
    c: DistanceX(g3,g3) = 5.35
    c: Coincident(g4,g5)
    c: Coincident(g5,g6)
    c: Coincident(g6,g7)
    c: Coincident(g7,g4)
    c: Horizontal(g4)
    c: Horizontal(g6)
    c: Vertical(g5)
    c: Vertical(g7)
    c: Coincident(g4,g1)
    c: Coincident(g5,g-9)
    c: Coincident(g8,g9)
    c: Coincident(g9,g10)
    c: Coincident(g10,g11)
    c: Coincident(g11,g8)
    c: Vertical(g8)
    c: Vertical(g10)
    c: Horizontal(g9)
    c: Horizontal(g11)
    c: Coincident(g8,g2)
    c: Coincident(g9,g-7)
FEATURE [PartDesign::Pad] Pad008
  BaseFeature = -> Pad007
  Direction = (0,0,1)
  Length = 0.5
  Length2 = 10
  Profile = -> Sketch011
  ReferenceAxis = -> Sketch011 [N_Axis]
  Refine = true
  Suppressed = false
  Type = 0
FEATURE [PartDesign::Body] Body006  label="Hailo Connector"
  AllowCompound = false
  Group = -> [Sketch009,Pad006,Sketch010,Pad007,Sketch011,Pad008]
  Origin = -> Origin012
  Tip = -> Pad008
FEATURE [Sketcher::SketchObject] Sketch012
  ArcFitTolerance = 1e-06
  AttachmentSupport = -> [XY_Plane013]
  FullyConstrained = true
  MakeInternals = false
  MapMode = 5
  sketch-geometry (6):
    g0: LineSegment StartX=-25.65 StartY=2.5 StartZ=0 EndX=-25.65 EndY=-2.5 EndZ=0
    g1: LineSegment StartX=-25.65 StartY=-2.5 StartZ=0 EndX=25.65 EndY=-2.5 EndZ=0
    g2: LineSegment StartX=25.65 StartY=-2.5 StartZ=0 EndX=25.65 EndY=2.5 EndZ=0
    g3: LineSegment StartX=25.65 StartY=2.5 StartZ=0 EndX=-25.65 EndY=2.5 EndZ=0
    g4: GeomPoint X=0 Y=2.5 Z=0
    g5: GeomPoint X=-25.65 Y=0 Z=0
  constraints (14):
    c: Coincident(g0,g1)
    c: Coincident(g1,g2)
    c: Coincident(g2,g3)
    c: Coincident(g3,g0)
    c: Vertical(g0)
    c: Vertical(g2)
    c: Horizontal(g1)
    c: Horizontal(g3)
    c: DistanceX(g3,g3) = 51.3
    c: DistanceY(g0,g0) = 5
    c: Symmetric(g3,g3,g4)
    c: Symmetric(g0,g0,g5)
    c: Vertical(g4,g-1)
    c: Horizontal(g-1,g5)
FEATURE [PartDesign::Pad] Pad009
  Direction = (0,0,1)
  Length = 3.5
  Length2 = 10
  Profile = -> Sketch012
  ReferenceAxis = -> Sketch012 [N_Axis]
  Refine = true
  Suppressed = false
  Type = 0
FEATURE [Sketcher::SketchObject] Sketch013
  ArcFitTolerance = 1e-06
  AttachmentSupport = -> [Pad009]
  ExternalGeometry = -> [Pad009]
  FullyConstrained = true
  MakeInternals = false
  MapMode = 5
  Placement = pos=(0,0,3.5) rot=(0,0,1;0rad)
  sketch-geometry (160):
    g0: LineSegment StartX=13.35 StartY=-0.9 StartZ=0 EndX=13.35 EndY=-1.5 EndZ=0
    g1: LineSegment StartX=13.35 StartY=-1.5 StartZ=0 EndX=13.95 EndY=-1.5 EndZ=0
    g2: LineSegment StartX=13.95 StartY=-1.5 StartZ=0 EndX=13.95 EndY=-0.9 EndZ=0
    g3: LineSegment StartX=13.95 StartY=-0.9 StartZ=0 EndX=13.35 EndY=-0.9 EndZ=0
    g4: LineSegment StartX=13.35 StartY=1.6 StartZ=0 EndX=13.35 EndY=1 EndZ=0
    g5: LineSegment StartX=13.35 StartY=1 StartZ=0 EndX=13.95 EndY=1 EndZ=0
    g6: LineSegment StartX=13.95 StartY=1 StartZ=0 EndX=13.95 EndY=1.6 EndZ=0
    g7: LineSegment StartX=13.95 StartY=1.6 StartZ=0 EndX=13.35 EndY=1.6 EndZ=0
    g8: LineSegment StartX=10.85 StartY=-0.9 StartZ=0 EndX=10.85 EndY=-1.5 EndZ=0
    g9: LineSegment StartX=10.85 StartY=-1.5 StartZ=0 EndX=11.45 EndY=-1.5 EndZ=0
    g10: LineSegment StartX=11.45 StartY=-1.5 StartZ=0 EndX=11.45 EndY=-0.9 EndZ=0
    g11: LineSegment StartX=11.45 StartY=-0.9 StartZ=0 EndX=10.85 EndY=-0.9 EndZ=0
    g12: LineSegment StartX=10.85 StartY=1.6 StartZ=0 EndX=10.85 EndY=1 EndZ=0
    g13: LineSegment StartX=10.85 StartY=1 StartZ=0 EndX=11.45 EndY=1 EndZ=0
    g14: LineSegment StartX=11.45 StartY=1 StartZ=0 EndX=11.45 EndY=1.6 EndZ=0
    g15: LineSegment StartX=11.45 StartY=1.6 StartZ=0 EndX=10.85 EndY=1.6 EndZ=0
    g16: LineSegment StartX=8.35 StartY=-0.9 StartZ=0 EndX=8.35 EndY=-1.5 EndZ=0
    g17: LineSegment StartX=8.35 StartY=-1.5 StartZ=0 EndX=8.95 EndY=-1.5 EndZ=0
    g18: LineSegment StartX=8.95 StartY=-1.5 StartZ=0 EndX=8.95 EndY=-0.9 EndZ=0
    g19: LineSegment StartX=8.95 StartY=-0.9 StartZ=0 EndX=8.35 EndY=-0.9 EndZ=0
    g20: LineSegment StartX=8.35 StartY=1.6 StartZ=0 EndX=8.35 EndY=1 EndZ=0
    g21: LineSegment StartX=8.35 StartY=1 StartZ=0 EndX=8.95 EndY=1 EndZ=0
    g22: LineSegment StartX=8.95 StartY=1 StartZ=0 EndX=8.95 EndY=1.6 EndZ=0
    g23: LineSegment StartX=8.95 StartY=1.6 StartZ=0 EndX=8.35 EndY=1.6 EndZ=0
    g24: LineSegment StartX=5.85 StartY=-0.9 StartZ=0 EndX=5.85 EndY=-1.5 EndZ=0
    g25: LineSegment StartX=5.85 StartY=-1.5 StartZ=0 EndX=6.45 EndY=-1.5 EndZ=0
    g26: LineSegment StartX=6.45 StartY=-1.5 StartZ=0 EndX=6.45 EndY=-0.9 EndZ=0
    g27: LineSegment StartX=6.45 StartY=-0.9 StartZ=0 EndX=5.85 EndY=-0.9 EndZ=0
    g28: LineSegment StartX=5.85 StartY=1.6 StartZ=0 EndX=5.85 EndY=1 EndZ=0
    g29: LineSegment StartX=5.85 StartY=1 StartZ=0 EndX=6.45 EndY=1 EndZ=0
    g30: LineSegment StartX=6.45 StartY=1 StartZ=0 EndX=6.45 EndY=1.6 EndZ=0
    g31: LineSegment StartX=6.45 StartY=1.6 StartZ=0 EndX=5.85 EndY=1.6 EndZ=0
    g32: LineSegment StartX=3.35 StartY=-0.9 StartZ=0 EndX=3.35 EndY=-1.5 EndZ=0
    g33: LineSegment StartX=3.35 StartY=-1.5 StartZ=0 EndX=3.95 EndY=-1.5 EndZ=0
    g34: LineSegment StartX=3.95 StartY=-1.5 StartZ=0 EndX=3.95 EndY=-0.9 EndZ=0
    g35: LineSegment StartX=3.95 StartY=-0.9 StartZ=0 EndX=3.35 EndY=-0.9 EndZ=0
    g36: LineSegment StartX=3.35 StartY=1.6 StartZ=0 EndX=3.35 EndY=1 EndZ=0
    g37: LineSegment StartX=3.35 StartY=1 StartZ=0 EndX=3.95 EndY=1 EndZ=0
    g38: LineSegment StartX=3.95 StartY=1 StartZ=0 EndX=3.95 EndY=1.6 EndZ=0
    g39: LineSegment StartX=3.95 StartY=1.6 StartZ=0 EndX=3.35 EndY=1.6 EndZ=0
    g40: LineSegment StartX=0.85 StartY=-0.9 StartZ=0 EndX=0.85 EndY=-1.5 EndZ=0
    g41: LineSegment StartX=0.85 StartY=-1.5 StartZ=0 EndX=1.45 EndY=-1.5 EndZ=0
    g42: LineSegment StartX=1.45 StartY=-1.5 StartZ=0 EndX=1.45 EndY=-0.9 EndZ=0
    g43: LineSegment StartX=1.45 StartY=-0.9 StartZ=0 EndX=0.85 EndY=-0.9 EndZ=0
    g44: LineSegment StartX=0.85 StartY=1.6 StartZ=0 EndX=0.85 EndY=1 EndZ=0
    g45: LineSegment StartX=0.85 StartY=1 StartZ=0 EndX=1.45 EndY=1 EndZ=0
    g46: LineSegment StartX=1.45 StartY=1 StartZ=0 EndX=1.45 EndY=1.6 EndZ=0
    g47: LineSegment StartX=1.45 StartY=1.6 StartZ=0 EndX=0.85 EndY=1.6 EndZ=0
    g48: LineSegment StartX=-1.65 StartY=-0.9 StartZ=0 EndX=-1.65 EndY=-1.5 EndZ=0
    g49: LineSegment StartX=-1.65 StartY=-1.5 StartZ=0 EndX=-1.05 EndY=-1.5 EndZ=0
    g50: LineSegment StartX=-1.05 StartY=-1.5 StartZ=0 EndX=-1.05 EndY=-0.9 EndZ=0
    g51: LineSegment StartX=-1.05 StartY=-0.9 StartZ=0 EndX=-1.65 EndY=-0.9 EndZ=0
    g52: LineSegment StartX=-1.65 StartY=1.6 StartZ=0 EndX=-1.65 EndY=1 EndZ=0
    g53: LineSegment StartX=-1.65 StartY=1 StartZ=0 EndX=-1.05 EndY=1 EndZ=0
    g54: LineSegment StartX=-1.05 StartY=1 StartZ=0 EndX=-1.05 EndY=1.6 EndZ=0
    g55: LineSegment StartX=-1.05 StartY=1.6 StartZ=0 EndX=-1.65 EndY=1.6 EndZ=0
    g56: LineSegment StartX=-4.15 StartY=-0.9 StartZ=0 EndX=-4.15 EndY=-1.5 EndZ=0
    g57: LineSegment StartX=-4.15 StartY=-1.5 StartZ=0 EndX=-3.55 EndY=-1.5 EndZ=0
    g58: LineSegment StartX=-3.55 StartY=-1.5 StartZ=0 EndX=-3.55 EndY=-0.9 EndZ=0
    g59: LineSegment StartX=-3.55 StartY=-0.9 StartZ=0 EndX=-4.15 EndY=-0.9 EndZ=0
    g60: LineSegment StartX=-4.15 StartY=1.6 StartZ=0 EndX=-4.15 EndY=1 EndZ=0
    g61: LineSegment StartX=-4.15 StartY=1 StartZ=0 EndX=-3.55 EndY=1 EndZ=0
    g62: LineSegment StartX=-3.55 StartY=1 StartZ=0 EndX=-3.55 EndY=1.6 EndZ=0
    g63: LineSegment StartX=-3.55 StartY=1.6 StartZ=0 EndX=-4.15 EndY=1.6 EndZ=0
    g64: LineSegment StartX=-6.65 StartY=-0.9 StartZ=0 EndX=-6.65 EndY=-1.5 EndZ=0
    g65: LineSegment StartX=-6.65 StartY=-1.5 StartZ=0 EndX=-6.05 EndY=-1.5 EndZ=0
    g66: LineSegment StartX=-6.05 StartY=-1.5 StartZ=0 EndX=-6.05 EndY=-0.9 EndZ=0
    g67: LineSegment StartX=-6.05 StartY=-0.9 StartZ=0 EndX=-6.65 EndY=-0.9 EndZ=0
    g68: LineSegment StartX=-6.65 StartY=1.6 StartZ=0 EndX=-6.65 EndY=1 EndZ=0
    g69: LineSegment StartX=-6.65 StartY=1 StartZ=0 EndX=-6.05 EndY=1 EndZ=0
    g70: LineSegment StartX=-6.05 StartY=1 StartZ=0 EndX=-6.05 EndY=1.6 EndZ=0
    g71: LineSegment StartX=-6.05 StartY=1.6 StartZ=0 EndX=-6.65 EndY=1.6 EndZ=0
    g72: LineSegment StartX=-9.15 StartY=-0.9 StartZ=0 EndX=-9.15 EndY=-1.5 EndZ=0
    g73: LineSegment StartX=-9.15 StartY=-1.5 StartZ=0 EndX=-8.55 EndY=-1.5 EndZ=0
    g74: LineSegment StartX=-8.55 StartY=-1.5 StartZ=0 EndX=-8.55 EndY=-0.9 EndZ=0
    g75: LineSegment StartX=-8.55 StartY=-0.9 StartZ=0 EndX=-9.15 EndY=-0.9 EndZ=0
    g76: LineSegment StartX=-9.15 StartY=1.6 StartZ=0 EndX=-9.15 EndY=1 EndZ=0
    g77: LineSegment StartX=-9.15 StartY=1 StartZ=0 EndX=-8.55 EndY=1 EndZ=0
    g78: LineSegment StartX=-8.55 StartY=1 StartZ=0 EndX=-8.55 EndY=1.6 EndZ=0
    g79: LineSegment StartX=-8.55 StartY=1.6 StartZ=0 EndX=-9.15 EndY=1.6 EndZ=0
    g80: LineSegment StartX=-11.65 StartY=-0.9 StartZ=0 EndX=-11.65 EndY=-1.5 EndZ=0
    g81: LineSegment StartX=-11.65 StartY=-1.5 StartZ=0 EndX=-11.05 EndY=-1.5 EndZ=0
    g82: LineSegment StartX=-11.05 StartY=-1.5 StartZ=0 EndX=-11.05 EndY=-0.9 EndZ=0
    g83: LineSegment StartX=-11.05 StartY=-0.9 StartZ=0 EndX=-11.65 EndY=-0.9 EndZ=0
    g84: LineSegment StartX=-11.65 StartY=1.6 StartZ=0 EndX=-11.65 EndY=1 EndZ=0
    g85: LineSegment StartX=-11.65 StartY=1 StartZ=0 EndX=-11.05 EndY=1 EndZ=0
    g86: LineSegment StartX=-11.05 StartY=1 StartZ=0 EndX=-11.05 EndY=1.6 EndZ=0
    g87: LineSegment StartX=-11.05 StartY=1.6 StartZ=0 EndX=-11.65 EndY=1.6 EndZ=0
    g88: LineSegment StartX=-14.15 StartY=-0.9 StartZ=0 EndX=-14.15 EndY=-1.5 EndZ=0
    g89: LineSegment StartX=-14.15 StartY=-1.5 StartZ=0 EndX=-13.55 EndY=-1.5 EndZ=0
    g90: LineSegment StartX=-13.55 StartY=-1.5 StartZ=0 EndX=-13.55 EndY=-0.9 EndZ=0
    g91: LineSegment StartX=-13.55 StartY=-0.9 StartZ=0 EndX=-14.15 EndY=-0.9 EndZ=0
    g92: LineSegment StartX=-14.15 StartY=1.6 StartZ=0 EndX=-14.15 EndY=1 EndZ=0
    g93: LineSegment StartX=-14.15 StartY=1 StartZ=0 EndX=-13.55 EndY=1 EndZ=0
    g94: LineSegment StartX=-13.55 StartY=1 StartZ=0 EndX=-13.55 EndY=1.6 EndZ=0
    g95: LineSegment StartX=-13.55 StartY=1.6 StartZ=0 EndX=-14.15 EndY=1.6 EndZ=0
    g96: LineSegment StartX=-16.65 StartY=-0.9 StartZ=0 EndX=-16.65 EndY=-1.5 EndZ=0
    g97: LineSegment StartX=-16.65 StartY=-1.5 StartZ=0 EndX=-16.05 EndY=-1.5 EndZ=0
    g98: LineSegment StartX=-16.05 StartY=-1.5 StartZ=0 EndX=-16.05 EndY=-0.9 EndZ=0
    g99: LineSegment StartX=-16.05 StartY=-0.9 StartZ=0 EndX=-16.65 EndY=-0.9 EndZ=0
    g100: LineSegment StartX=-16.65 StartY=1.6 StartZ=0 EndX=-16.65 EndY=1 EndZ=0
    g101: LineSegment StartX=-16.65 StartY=1 StartZ=0 EndX=-16.05 EndY=1 EndZ=0
    g102: LineSegment StartX=-16.05 StartY=1 StartZ=0 EndX=-16.05 EndY=1.6 EndZ=0
    g103: LineSegment StartX=-16.05 StartY=1.6 StartZ=0 EndX=-16.65 EndY=1.6 EndZ=0
    g104: LineSegment StartX=-19.15 StartY=-0.9 StartZ=0 EndX=-19.15 EndY=-1.5 EndZ=0
    g105: LineSegment StartX=-19.15 StartY=-1.5 StartZ=0 EndX=-18.55 EndY=-1.5 EndZ=0
    g106: LineSegment StartX=-18.55 StartY=-1.5 StartZ=0 EndX=-18.55 EndY=-0.9 EndZ=0
    g107: LineSegment StartX=-18.55 StartY=-0.9 StartZ=0 EndX=-19.15 EndY=-0.9 EndZ=0
    g108: LineSegment StartX=-19.15 StartY=1.6 StartZ=0 EndX=-19.15 EndY=1 EndZ=0
    g109: LineSegment StartX=-19.15 StartY=1 StartZ=0 EndX=-18.55 EndY=1 EndZ=0
    g110: LineSegment StartX=-18.55 StartY=1 StartZ=0 EndX=-18.55 EndY=1.6 EndZ=0
    g111: LineSegment StartX=-18.55 StartY=1.6 StartZ=0 EndX=-19.15 EndY=1.6 EndZ=0
    g112: LineSegment StartX=-21.65 StartY=-0.9 StartZ=0 EndX=-21.65 EndY=-1.5 EndZ=0
    g113: LineSegment StartX=-21.65 StartY=-1.5 StartZ=0 EndX=-21.05 EndY=-1.5 EndZ=0
    g114: LineSegment StartX=-21.05 StartY=-1.5 StartZ=0 EndX=-21.05 EndY=-0.9 EndZ=0
    g115: LineSegment StartX=-21.05 StartY=-0.9 StartZ=0 EndX=-21.65 EndY=-0.9 EndZ=0
    g116: LineSegment StartX=-21.65 StartY=1.6 StartZ=0 EndX=-21.65 EndY=1 EndZ=0
    g117: LineSegment StartX=-21.65 StartY=1 StartZ=0 EndX=-21.05 EndY=1 EndZ=0
    g118: LineSegment StartX=-21.05 StartY=1 StartZ=0 EndX=-21.05 EndY=1.6 EndZ=0
    g119: LineSegment StartX=-21.05 StartY=1.6 StartZ=0 EndX=-21.65 EndY=1.6 EndZ=0
    g120: LineSegment StartX=-24.15 StartY=-0.9 StartZ=0 EndX=-24.15 EndY=-1.5 EndZ=0
    g121: LineSegment StartX=-24.15 StartY=-1.5 StartZ=0 EndX=-23.55 EndY=-1.5 EndZ=0
    g122: LineSegment StartX=-23.55 StartY=-1.5 StartZ=0 EndX=-23.55 EndY=-0.9 EndZ=0
    g123: LineSegment StartX=-23.55 StartY=-0.9 StartZ=0 EndX=-24.15 EndY=-0.9 EndZ=0
    g124: LineSegment StartX=-24.15 StartY=1.6 StartZ=0 EndX=-24.15 EndY=1 EndZ=0
    g125: LineSegment StartX=-24.15 StartY=1 StartZ=0 EndX=-23.55 EndY=1 EndZ=0
    g126: LineSegment StartX=-23.55 StartY=1 StartZ=0 EndX=-23.55 EndY=1.6 EndZ=0
    g127: LineSegment StartX=-23.55 StartY=1.6 StartZ=0 EndX=-24.15 EndY=1.6 EndZ=0
    g128: LineSegment StartX=23.35 StartY=-0.9 StartZ=0 EndX=23.35 EndY=-1.5 EndZ=0
    g129: LineSegment StartX=23.35 StartY=-1.5 StartZ=0 EndX=23.95 EndY=-1.5 EndZ=0
    g130: LineSegment StartX=23.95 StartY=-1.5 StartZ=0 EndX=23.95 EndY=-0.9 EndZ=0
    g131: LineSegment StartX=23.95 StartY=-0.9 StartZ=0 EndX=23.35 EndY=-0.9 EndZ=0
    g132: LineSegment StartX=23.35 StartY=1.6 StartZ=0 EndX=23.35 EndY=1 EndZ=0
    g133: LineSegment StartX=23.35 StartY=1 StartZ=0 EndX=23.95 EndY=1 EndZ=0
    g134: LineSegment StartX=23.95 StartY=1 StartZ=0 EndX=23.95 EndY=1.6 EndZ=0
    g135: LineSegment StartX=23.95 StartY=1.6 StartZ=0 EndX=23.35 EndY=1.6 EndZ=0
    g136: LineSegment StartX=20.85 StartY=-0.9 StartZ=0 EndX=20.85 EndY=-1.5 EndZ=0
    g137: LineSegment StartX=20.85 StartY=-1.5 StartZ=0 EndX=21.45 EndY=-1.5 EndZ=0
    g138: LineSegment StartX=21.45 StartY=-1.5 StartZ=0 EndX=21.45 EndY=-0.9 EndZ=0
    g139: LineSegment StartX=21.45 StartY=-0.9 StartZ=0 EndX=20.85 EndY=-0.9 EndZ=0
    g140: LineSegment StartX=20.85 StartY=1.6 StartZ=0 EndX=20.85 EndY=1 EndZ=0
    g141: LineSegment StartX=20.85 StartY=1 StartZ=0 EndX=21.45 EndY=1 EndZ=0
    g142: LineSegment StartX=21.45 StartY=1 StartZ=0 EndX=21.45 EndY=1.6 EndZ=0
    g143: LineSegment StartX=21.45 StartY=1.6 StartZ=0 EndX=20.85 EndY=1.6 EndZ=0
    g144: LineSegment StartX=18.35 StartY=-0.9 StartZ=0 EndX=18.35 EndY=-1.5 EndZ=0
    g145: LineSegment StartX=18.35 StartY=-1.5 StartZ=0 EndX=18.95 EndY=-1.5 EndZ=0
    g146: LineSegment StartX=18.95 StartY=-1.5 StartZ=0 EndX=18.95 EndY=-0.9 EndZ=0
    g147: LineSegment StartX=18.95 StartY=-0.9 StartZ=0 EndX=18.35 EndY=-0.9 EndZ=0
    g148: LineSegment StartX=18.35 StartY=1.6 StartZ=0 EndX=18.35 EndY=1 EndZ=0
    g149: LineSegment StartX=18.35 StartY=1 StartZ=0 EndX=18.95 EndY=1 EndZ=0
    g150: LineSegment StartX=18.95 StartY=1 StartZ=0 EndX=18.95 EndY=1.6 EndZ=0
    g151: LineSegment StartX=18.95 StartY=1.6 StartZ=0 EndX=18.35 EndY=1.6 EndZ=0
    g152: LineSegment StartX=15.85 StartY=-0.9 StartZ=0 EndX=15.85 EndY=-1.5 EndZ=0
    g153: LineSegment StartX=15.85 StartY=-1.5 StartZ=0 EndX=16.45 EndY=-1.5 EndZ=0
    g154: LineSegment StartX=16.45 StartY=-1.5 StartZ=0 EndX=16.45 EndY=-0.9 EndZ=0
    g155: LineSegment StartX=16.45 StartY=-0.9 StartZ=0 EndX=15.85 EndY=-0.9 EndZ=0
    g156: LineSegment StartX=15.85 StartY=1.6 StartZ=0 EndX=15.85 EndY=1 EndZ=0
    g157: LineSegment StartX=15.85 StartY=1 StartZ=0 EndX=16.45 EndY=1 EndZ=0
    g158: LineSegment StartX=16.45 StartY=1 StartZ=0 EndX=16.45 EndY=1.6 EndZ=0
    g159: LineSegment StartX=16.45 StartY=1.6 StartZ=0 EndX=15.85 EndY=1.6 EndZ=0
  constraints (480):
    c: Coincident(g0,g1)
    c: Coincident(g1,g2)
    c: Coincident(g2,g3)
    c: Coincident(g3,g0)
    c: Vertical(g0)
    c: Vertical(g2)
    c: Horizontal(g1)
    c: Horizontal(g3)
    c: DistanceX(g3,g3) = 0.6
    c: DistanceY(g2,g2) = 0.6
    c: Coincident(g4,g5)
    c: Coincident(g5,g6)
    c: Coincident(g6,g7)
    c: Coincident(g7,g4)
    c: Vertical(g4)
    c: Vertical(g6)
    c: Horizontal(g5)
    c: Horizontal(g7)
    c: DistanceX(g7,g7) = 0.6
    c: DistanceY(g6,g6) = 0.6
    c: Vertical(g4,g0)
    c: Distance(g3,g5) = 1.9
    c: Coincident(g8,g9)
    c: Coincident(g9,g10)
    c: Coincident(g10,g11)
    c: Coincident(g11,g8)
    c: Vertical(g8)
    c: Vertical(g10)
    c: Horizontal(g9)
    c: Horizontal(g11)
    c: DistanceX(g11,g11) = 0.6
    c: DistanceY(g10,g10) = 0.6
    c: Coincident(g12,g13)
    c: Coincident(g13,g14)
    c: Coincident(g14,g15)
    c: Coincident(g15,g12)
    c: Vertical(g12)
    c: Vertical(g14)
    c: Horizontal(g13)
    c: Horizontal(g15)
    c: DistanceX(g15,g15) = 0.6
    c: DistanceY(g14,g14) = 0.6
    c: Vertical(g12,g8)
    c: Distance(g11,g13) = 1.9
    c: Horizontal(g4,g14)
    c: Distance(g14,g4) = 1.9
    c: Coincident(g16,g17)
    c: Coincident(g17,g18)
    c: Coincident(g18,g19)
    c: Coincident(g19,g16)
    c: Vertical(g16)
    c: Vertical(g18)
    c: Horizontal(g17)
    c: Horizontal(g19)
    c: DistanceX(g19,g19) = 0.6
    c: DistanceY(g18,g18) = 0.6
    c: Coincident(g20,g21)
    c: Coincident(g21,g22)
    c: Coincident(g22,g23)
    c: Coincident(g23,g20)
    c: Vertical(g20)
    c: Vertical(g22)
    c: Horizontal(g21)
    c: Horizontal(g23)
    c: DistanceX(g23,g23) = 0.6
    c: DistanceY(g22,g22) = 0.6
    c: Vertical(g20,g16)
    c: Distance(g19,g21) = 1.9
    c: Coincident(g24,g25)
    c: Coincident(g25,g26)
    c: Coincident(g26,g27)
    c: Coincident(g27,g24)
    c: Vertical(g24)
    c: Vertical(g26)
    c: Horizontal(g25)
    c: Horizontal(g27)
    c: DistanceX(g27,g27) = 0.6
    c: DistanceY(g26,g26) = 0.6
    c: Coincident(g28,g29)
    c: Coincident(g29,g30)
    c: Coincident(g30,g31)
    c: Coincident(g31,g28)
    c: Vertical(g28)
    c: Vertical(g30)
    c: Horizontal(g29)
    c: Horizontal(g31)
    c: DistanceX(g31,g31) = 0.6
    c: DistanceY(g30,g30) = 0.6
    c: Vertical(g28,g24)
    c: Distance(g27,g29) = 1.9
    c: Horizontal(g20,g30)
    c: Distance(g30,g20) = 1.9
    c: Horizontal(g8,g17)
    c: Distance(g18,g8) = 1.9
    c: Coincident(g32,g33)
    c: Coincident(g33,g34)
    c: Coincident(g34,g35)
    c: Coincident(g35,g32)
    c: Vertical(g32)
    c: Vertical(g34)
    c: Horizontal(g33)
    c: Horizontal(g35)
    c: DistanceX(g35,g35) = 0.6
    c: DistanceY(g34,g34) = 0.6
    c: Coincident(g36,g37)
    c: Coincident(g37,g38)
    c: Coincident(g38,g39)
    c: Coincident(g39,g36)
    c: Vertical(g36)
    c: Vertical(g38)
    c: Horizontal(g37)
    c: Horizontal(g39)
    c: DistanceX(g39,g39) = 0.6
    c: DistanceY(g38,g38) = 0.6
    c: Vertical(g36,g32)
    c: Distance(g35,g37) = 1.9
    c: Coincident(g40,g41)
    c: Coincident(g41,g42)
    c: Coincident(g42,g43)
    c: Coincident(g43,g40)
    c: Vertical(g40)
    c: Vertical(g42)
    c: Horizontal(g41)
    c: Horizontal(g43)
    c: DistanceX(g43,g43) = 0.6
    c: DistanceY(g42,g42) = 0.6
    c: Coincident(g44,g45)
    c: Coincident(g45,g46)
    c: Coincident(g46,g47)
    c: Coincident(g47,g44)
    c: Vertical(g44)
    c: Vertical(g46)
    c: Horizontal(g45)
    c: Horizontal(g47)
    c: DistanceX(g47,g47) = 0.6
    c: DistanceY(g46,g46) = 0.6
    c: Vertical(g44,g40)
    c: Distance(g43,g45) = 1.9
    c: Horizontal(g36,g46)
    c: Distance(g46,g36) = 1.9
    c: Coincident(g48,g49)
    c: Coincident(g49,g50)
    c: Coincident(g50,g51)
    c: Coincident(g51,g48)
    c: Vertical(g48)
    c: Vertical(g50)
    c: Horizontal(g49)
    c: Horizontal(g51)
    c: DistanceX(g51,g51) = 0.6
    c: DistanceY(g50,g50) = 0.6
    c: Coincident(g52,g53)
    c: Coincident(g53,g54)
    c: Coincident(g54,g55)
    c: Coincident(g55,g52)
    c: Vertical(g52)
    c: Vertical(g54)
    c: Horizontal(g53)
    c: Horizontal(g55)
    c: DistanceX(g55,g55) = 0.6
    c: DistanceY(g54,g54) = 0.6
    c: Vertical(g52,g48)
    c: Distance(g51,g53) = 1.9
    c: Coincident(g56,g57)
    c: Coincident(g57,g58)
    c: Coincident(g58,g59)
    c: Coincident(g59,g56)
    c: Vertical(g56)
    c: Vertical(g58)
    c: Horizontal(g57)
    c: Horizontal(g59)
    c: DistanceX(g59,g59) = 0.6
    c: DistanceY(g58,g58) = 0.6
    c: Coincident(g60,g61)
    c: Coincident(g61,g62)
    c: Coincident(g62,g63)
    c: Coincident(g63,g60)
    c: Vertical(g60)
    c: Vertical(g62)
    c: Horizontal(g61)
    c: Horizontal(g63)
    c: DistanceX(g63,g63) = 0.6
    c: DistanceY(g62,g62) = 0.6
    c: Vertical(g60,g56)
    c: Distance(g59,g61) = 1.9
    c: Horizontal(g52,g62)
    c: Distance(g62,g52) = 1.9
    c: Horizontal(g40,g49)
    c: Distance(g50,g40) = 1.9
    c: Horizontal(g24,g33)
    c: Distance(g24,g34) = 1.9
    c: Coincident(g64,g65)
    c: Coincident(g65,g66)
    c: Coincident(g66,g67)
    c: Coincident(g67,g64)
    c: Vertical(g64)
    c: Vertical(g66)
    c: Horizontal(g65)
    c: Horizontal(g67)
    c: DistanceX(g67,g67) = 0.6
    c: DistanceY(g66,g66) = 0.6
    c: Coincident(g68,g69)
    c: Coincident(g69,g70)
    c: Coincident(g70,g71)
    c: Coincident(g71,g68)
    c: Vertical(g68)
    c: Vertical(g70)
    c: Horizontal(g69)
    c: Horizontal(g71)
    c: DistanceX(g71,g71) = 0.6
    c: DistanceY(g70,g70) = 0.6
    c: Vertical(g68,g64)
    c: Distance(g67,g69) = 1.9
    c: Coincident(g72,g73)
    c: Coincident(g73,g74)
    c: Coincident(g74,g75)
    c: Coincident(g75,g72)
    c: Vertical(g72)
    c: Vertical(g74)
    c: Horizontal(g73)
    c: Horizontal(g75)
    c: DistanceX(g75,g75) = 0.6
    c: DistanceY(g74,g74) = 0.6
    c: Coincident(g76,g77)
    c: Coincident(g77,g78)
    c: Coincident(g78,g79)
    c: Coincident(g79,g76)
    c: Vertical(g76)
    c: Vertical(g78)
    c: Horizontal(g77)
    c: Horizontal(g79)
    c: DistanceX(g79,g79) = 0.6
    c: DistanceY(g78,g78) = 0.6
    c: Vertical(g76,g72)
    c: Distance(g75,g77) = 1.9
    c: Horizontal(g68,g78)
    c: Distance(g78,g68) = 1.9
    c: Coincident(g80,g81)
    c: Coincident(g81,g82)
    c: Coincident(g82,g83)
    c: Coincident(g83,g80)
    c: Vertical(g80)
    c: Vertical(g82)
    c: Horizontal(g81)
    c: Horizontal(g83)
    c: DistanceX(g83,g83) = 0.6
    c: DistanceY(g82,g82) = 0.6
    c: Coincident(g84,g85)
    c: Coincident(g85,g86)
    c: Coincident(g86,g87)
    c: Coincident(g87,g84)
    c: Vertical(g84)
    c: Vertical(g86)
    c: Horizontal(g85)
    c: Horizontal(g87)
    c: DistanceX(g87,g87) = 0.6
    c: DistanceY(g86,g86) = 0.6
    c: Vertical(g84,g80)
    c: Distance(g83,g85) = 1.9
    c: Coincident(g88,g89)
    c: Coincident(g89,g90)
    c: Coincident(g90,g91)
    c: Coincident(g91,g88)
    c: Vertical(g88)
    c: Vertical(g90)
    c: Horizontal(g89)
    c: Horizontal(g91)
    c: DistanceX(g91,g91) = 0.6
    c: DistanceY(g90,g90) = 0.6
    c: Coincident(g92,g93)
    c: Coincident(g93,g94)
    c: Coincident(g94,g95)
    c: Coincident(g95,g92)
    c: Vertical(g92)
    c: Vertical(g94)
    c: Horizontal(g93)
    c: Horizontal(g95)
    c: DistanceX(g95,g95) = 0.6
    c: DistanceY(g94,g94) = 0.6
    c: Vertical(g92,g88)
    c: Distance(g91,g93) = 1.9
    c: Horizontal(g84,g94)
    c: Distance(g94,g84) = 1.9
    c: Horizontal(g72,g81)
    c: Distance(g82,g72) = 1.9
    c: Coincident(g96,g97)
    c: Coincident(g97,g98)
    c: Coincident(g98,g99)
    c: Coincident(g99,g96)
    c: Vertical(g96)
    c: Vertical(g98)
    c: Horizontal(g97)
    c: Horizontal(g99)
    c: DistanceX(g99,g99) = 0.6
    c: DistanceY(g98,g98) = 0.6
    c: Coincident(g100,g101)
    c: Coincident(g101,g102)
    c: Coincident(g102,g103)
    c: Coincident(g103,g100)
    c: Vertical(g100)
    c: Vertical(g102)
    c: Horizontal(g101)
    c: Horizontal(g103)
    c: DistanceX(g103,g103) = 0.6
    c: DistanceY(g102,g102) = 0.6
    c: Vertical(g100,g96)
    c: Distance(g99,g101) = 1.9
    c: Coincident(g104,g105)
    c: Coincident(g105,g106)
    c: Coincident(g106,g107)
    c: Coincident(g107,g104)
    c: Vertical(g104)
    c: Vertical(g106)
    c: Horizontal(g105)
    c: Horizontal(g107)
    c: DistanceX(g107,g107) = 0.6
    c: DistanceY(g106,g106) = 0.6
    c: Coincident(g108,g109)
    c: Coincident(g109,g110)
    c: Coincident(g110,g111)
    c: Coincident(g111,g108)
    c: Vertical(g108)
    c: Vertical(g110)
    c: Horizontal(g109)
    c: Horizontal(g111)
    c: DistanceX(g111,g111) = 0.6
    c: DistanceY(g110,g110) = 0.6
    c: Vertical(g108,g104)
    c: Distance(g107,g109) = 1.9
    c: Horizontal(g100,g110)
    c: Distance(g110,g100) = 1.9
    c: Coincident(g112,g113)
    c: Coincident(g113,g114)
    c: Coincident(g114,g115)
    c: Coincident(g115,g112)
    c: Vertical(g112)
    c: Vertical(g114)
    c: Horizontal(g113)
    c: Horizontal(g115)
    c: DistanceX(g115,g115) = 0.6
    c: DistanceY(g114,g114) = 0.6
    c: Coincident(g116,g117)
    c: Coincident(g117,g118)
    c: Coincident(g118,g119)
    c: Coincident(g119,g116)
    c: Vertical(g116)
    c: Vertical(g118)
    c: Horizontal(g117)
    c: Horizontal(g119)
    c: DistanceX(g119,g119) = 0.6
    c: DistanceY(g118,g118) = 0.6
    c: Vertical(g116,g112)
    c: Distance(g115,g117) = 1.9
    c: Coincident(g120,g121)
    c: Coincident(g121,g122)
    c: Coincident(g122,g123)
    c: Coincident(g123,g120)
    c: Vertical(g120)
    c: Vertical(g122)
    c: Horizontal(g121)
    c: Horizontal(g123)
    c: DistanceX(g123,g123) = 0.6
    c: DistanceY(g122,g122) = 0.6
    c: Coincident(g124,g125)
    c: Coincident(g125,g126)
    c: Coincident(g126,g127)
    c: Coincident(g127,g124)
    c: Vertical(g124)
    c: Vertical(g126)
    c: Horizontal(g125)
    c: Horizontal(g127)
    c: DistanceX(g127,g127) = 0.6
    c: DistanceY(g126,g126) = 0.6
    c: Vertical(g124,g120)
    c: Distance(g123,g125) = 1.9
    c: Horizontal(g116,g126)
    c: Distance(g126,g116) = 1.9
    c: Horizontal(g104,g113)
    c: Distance(g114,g104) = 1.9
    c: Horizontal(g88,g97)
    c: Distance(g88,g98) = 1.9
    c: Horizontal(g65,g56)
    c: Distance(g56,g66) = 1.9
    c: Coincident(g128,g129)
    c: Coincident(g129,g130)
    c: Coincident(g130,g131)
    c: Coincident(g131,g128)
    c: Vertical(g128)
    c: Vertical(g130)
    c: Horizontal(g129)
    c: Horizontal(g131)
    c: DistanceX(g131,g131) = 0.6
    c: DistanceY(g130,g130) = 0.6
    c: Coincident(g132,g133)
    c: Coincident(g133,g134)
    c: Coincident(g134,g135)
    c: Coincident(g135,g132)
    c: Vertical(g132)
    c: Vertical(g134)
    c: Horizontal(g133)
    c: Horizontal(g135)
    c: DistanceX(g135,g135) = 0.6
    c: DistanceY(g134,g134) = 0.6
    c: Vertical(g132,g128)
    c: Distance(g131,g133) = 1.9
    c: Coincident(g136,g137)
    c: Coincident(g137,g138)
    c: Coincident(g138,g139)
    c: Coincident(g139,g136)
    c: Vertical(g136)
    c: Vertical(g138)
    c: Horizontal(g137)
    c: Horizontal(g139)
    c: DistanceX(g139,g139) = 0.6
    c: DistanceY(g138,g138) = 0.6
    c: Coincident(g140,g141)
    c: Coincident(g141,g142)
    c: Coincident(g142,g143)
    c: Coincident(g143,g140)
    c: Vertical(g140)
    c: Vertical(g142)
    c: Horizontal(g141)
    c: Horizontal(g143)
    c: DistanceX(g143,g143) = 0.6
    c: DistanceY(g142,g142) = 0.6
    c: Vertical(g140,g136)
    c: Distance(g139,g141) = 1.9
    c: Horizontal(g132,g142)
    c: Distance(g142,g132) = 1.9
    c: Coincident(g144,g145)
    c: Coincident(g145,g146)
    c: Coincident(g146,g147)
    c: Coincident(g147,g144)
    c: Vertical(g144)
    c: Vertical(g146)
    c: Horizontal(g145)
    c: Horizontal(g147)
    c: DistanceX(g147,g147) = 0.6
    c: DistanceY(g146,g146) = 0.6
    c: Coincident(g148,g149)
    c: Coincident(g149,g150)
    c: Coincident(g150,g151)
    c: Coincident(g151,g148)
    c: Vertical(g148)
    c: Vertical(g150)
    c: Horizontal(g149)
    c: Horizontal(g151)
    c: DistanceX(g151,g151) = 0.6
    c: DistanceY(g150,g150) = 0.6
    c: Vertical(g148,g144)
    c: Distance(g147,g149) = 1.9
    c: Coincident(g152,g153)
    c: Coincident(g153,g154)
    c: Coincident(g154,g155)
    c: Coincident(g155,g152)
    c: Vertical(g152)
    c: Vertical(g154)
    c: Horizontal(g153)
    c: Horizontal(g155)
    c: DistanceX(g155,g155) = 0.6
    c: DistanceY(g154,g154) = 0.6
    c: Coincident(g156,g157)
    c: Coincident(g157,g158)
    c: Coincident(g158,g159)
    c: Coincident(g159,g156)
    c: Vertical(g156)
    c: Vertical(g158)
    c: Horizontal(g157)
    c: Horizontal(g159)
    c: DistanceX(g159,g159) = 0.6
    c: DistanceY(g158,g158) = 0.6
    c: Vertical(g156,g152)
    c: Distance(g155,g157) = 1.9
    c: Horizontal(g148,g158)
    c: Distance(g158,g148) = 1.9
    c: Horizontal(g136,g145)
    c: Distance(g146,g136) = 1.9
    c: Horizontal(g1,g152)
    c: Distance(g152,g2) = 1.9
    c: Distance(g-4,g120) = 1.5
    c: Distance(g-5,g121) = 1
FEATURE [PartDesign::Pocket] Pocket002
  BaseFeature = -> Pad009
  Direction = (0,0,-1)
  Length = 5
  Length2 = 5
  Profile = -> Sketch013
  ReferenceAxis = -> Sketch013 [N_Axis]
  Refine = true
  Suppressed = false
  Type = 0
FEATURE [PartDesign::Body] Body007  label="Pin Block"
  AllowCompound = false
  Group = -> [Sketch012,Pad009,Sketch013,Pocket002]
  Origin = -> Origin013
  Tip = -> Pocket002
FEATURE [App::Link] Board002  label="Board003"
  LinkedObject = -> Body004
FEATURE [App::FeaturePython] GroundedJoint001  # Assembly grounded joint (typed FeaturePython)
  ObjectToGround = -> Board002
FEATURE [App::Link] Hole_Inserts  label="Hole Inserts001"
  LinkPlacement = pos=(-23.6422,-29.0551,0) rot=(0,0,1;0rad)
  LinkedObject = -> Body005
  Placement = pos=(-23.6422,-29.0551,0) rot=(0,0,1;0rad)
FEATURE [App::Link] Hailo_Connector  label="Hailo Connector001"
  LinkPlacement = pos=(-13.9,1.8e-15,1.57) rot=(0,0,1;0rad)
  LinkedObject = -> Body006
  Placement = pos=(-13.9,1.8e-15,1.57) rot=(0,0,1;0rad)
FEATURE [App::Link] Pin_Block  label="Pin Block001"
  LinkPlacement = pos=(1.6e-15,24.25,1.57) rot=(0,0,1;0rad)
  LinkedObject = -> Body007
  Placement = pos=(1.6e-15,24.25,1.57) rot=(0,0,1;0rad)
FEATURE [App::Link] Hole_Inserts001  label="Hole Inserts002"
  LinkPlacement = pos=(34.3578,-29.0551,0) rot=(0,0,1;0rad)
  LinkedObject = -> Body005
  Placement = pos=(34.3578,-29.0551,0) rot=(0,0,1;0rad)
FEATURE [App::Link] Hole_Inserts002  label="Hole Inserts003"
  LinkPlacement = pos=(34.3578,20.4449,0) rot=(0,0,1;0rad)
  LinkedObject = -> Body005
  Placement = pos=(34.3578,20.4449,0) rot=(0,0,1;0rad)
FEATURE [App::Link] Hole_Inserts003  label="Hole Inserts004"
  LinkPlacement = pos=(-23.6422,20.4449,0) rot=(0,0,1;0rad)
  LinkedObject = -> Body005
  Placement = pos=(-23.6422,20.4449,0) rot=(0,0,1;0rad)
FEATURE [App::FeaturePython] Joint002  label="Fixed002"  # Assembly joint (typed FeaturePython)
  Activated = true
  AngleMax = 0
  AngleMin = 0
  Detach1 = false
  Detach2 = false
  Distance = 0
  Distance2 = 0
  EnableAngleMax = false
  EnableAngleMin = false
  EnableLengthMax = false
  EnableLengthMin = false
  JointType = 0 (Fixed)
  LengthMax = 0
  LengthMin = 0
  Placement1 = pos=(-2.48276,4.30507,1.57) rot=(0,0,1;0rad)
  Reference1 = -> Assembly002 [Hole_Inserts003.Vertex2,Hole_Inserts003.Vertex2]
FEATURE [PartDesign::Pad] Pad005
  Direction = (0,0,1)
  Length = 1.57
  Length2 = 10
  Profile = -> Sketch008
  ReferenceAxis = -> Sketch008 [N_Axis]
  Refine = true
  Suppressed = false
  Type = 0
FEATURE [PartDesign::Body] Body005  label="Hole Inserts"
  AllowCompound = false
  Group = -> [Sketch008,Pad005]
  Origin = -> Origin011
  Tip = -> Pad005
FEATURE [App::Part] Part001  label="M.2 HAT+"
  Group = -> [Body004,Body005,Body006,Body007]
  Origin = -> Origin006
FEATURE [App::FeaturePython] Joint003  label="Fixed003"  # Assembly joint (typed FeaturePython)
  Activated = true
  AngleMax = 0
  AngleMin = 0
  Detach1 = false
  Detach2 = false
  Distance = 0
  Distance2 = 0
  EnableAngleMax = false
  EnableAngleMin = false
  EnableLengthMax = false
  EnableLengthMin = false
  JointType = 0 (Fixed)
  LengthMax = 0
  LengthMin = 0
  Placement1 = pos=(-5.35776,4.30507,1.57) rot=(0,0,1;0rad)
  Placement2 = pos=(-29,24.75,1.57) rot=(0,0,1;0rad)
  Reference1 = -> Assembly002 [Hole_Inserts003.Edge3,Hole_Inserts003.Edge3]
  Reference2 = -> Assembly002 [Board002.Edge60,Board002.Edge60]
FEATURE [App::FeaturePython] Joint004  label="Fixed004"  # Assembly joint (typed FeaturePython)
  Activated = true
  AngleMax = 0
  AngleMin = 0
  Detach1 = false
  Detach2 = false
  Distance = 0
  Distance2 = 0
  EnableAngleMax = false
  EnableAngleMin = false
  EnableLengthMax = false
  EnableLengthMin = false
  JointType = 0 (Fixed)
  LengthMax = 0
  LengthMin = 0
  Placement1 = pos=(-5.35776,4.30507,1.57) rot=(0,0,1;0rad)
  Placement2 = pos=(29,24.75,1.57) rot=(0,0,1;0rad)
  Reference1 = -> Assembly002 [Hole_Inserts002.Edge3,Hole_Inserts002.Edge3]
  Reference2 = -> Assembly002 [Board002.Edge62,Board002.Edge62]
FEATURE [App::FeaturePython] Joint005  label="Fixed005"  # Assembly joint (typed FeaturePython)
  Activated = true
  AngleMax = 0
  AngleMin = 0
  Detach1 = false
  Detach2 = false
  Distance = 0
  Distance2 = 0
  EnableAngleMax = false
  EnableAngleMin = false
  EnableLengthMax = false
  EnableLengthMin = false
  JointType = 0 (Fixed)
  LengthMax = 0
  LengthMin = 0
  Placement1 = pos=(-5.35776,4.30507,1.57) rot=(0,0,1;0rad)
  Placement2 = pos=(29,-24.75,1.57) rot=(0,0,1;0rad)
  Reference1 = -> Assembly002 [Hole_Inserts001.Edge3,Hole_Inserts001.Edge3]
  Reference2 = -> Assembly002 [Board002.Edge59,Board002.Edge59]
FEATURE [App::FeaturePython] Joint006  label="Fixed006"  # Assembly joint (typed FeaturePython)
  Activated = true
  AngleMax = 0
  AngleMin = 0
  Detach1 = false
  Detach2 = false
  Distance = 0
  Distance2 = 0
  EnableAngleMax = false
  EnableAngleMin = false
  EnableLengthMax = false
  EnableLengthMin = false
  JointType = 0 (Fixed)
  LengthMax = 0
  LengthMin = 0
  Placement1 = pos=(-5.35776,4.30507,1.57) rot=(0,0,1;0rad)
  Placement2 = pos=(-29,-24.75,1.57) rot=(0,0,1;0rad)
  Reference1 = -> Assembly002 [Hole_Inserts.Edge3,Hole_Inserts.Edge3]
  Reference2 = -> Assembly002 [Board002.Edge58,Board002.Edge58]
FEATURE [App::FeaturePython] Joint007  label="Fixed007"  # Assembly joint (typed FeaturePython)
  Activated = true
  AngleMax = 0
  AngleMin = 0
  Detach1 = false
  Detach2 = false
  Distance = 0
  Distance2 = 0
  EnableAngleMax = false
  EnableAngleMin = false
  EnableLengthMax = false
  EnableLengthMin = false
  JointType = 0 (Fixed)
  LengthMax = 0
  LengthMin = 0
  Offset2 = pos=(0,1.5,0) rot=(0,0,1;3.14159rad)
  Placement1 = pos=(-1.6e-15,2.5,0) rot=(-0.707107,0,0.707107;3.14159rad)
  Placement2 = pos=(0,26.75,1.57) rot=(0,-1,0;4.71239rad)
  Reference1 = -> Assembly002 [Pin_Block.Edge6,Pin_Block.Edge6]
  Reference2 = -> Assembly002 [Board002.Edge4,Board002.Edge4]
FEATURE [App::FeaturePython] Joint008  label="Fixed008"  # Assembly joint (typed FeaturePython)
  Activated = true
  AngleMax = 0
  AngleMin = 0
  Detach1 = false
  Detach2 = false
  Distance = 0
  Distance2 = 0
  EnableAngleMax = false
  EnableAngleMin = false
  EnableLengthMax = false
  EnableLengthMin = false
  JointType = 0 (Fixed)
  LengthMax = 0
  LengthMin = 0
  Offset2 = pos=(0,-50,0) rot=(0,0,1;0rad)
  Placement1 = pos=(-3.6,0,0) rot=(-0.57735,-0.57735,0.57735;4.18879rad)
  Placement2 = pos=(-17.5,1.8e-15,1.57) rot=(-0.57735,-0.57735,0.57735;4.18879rad)
  Reference1 = -> Assembly002 [Hailo_Connector.Edge1,Hailo_Connector.Edge1]
  Reference2 = -> Assembly002 [Board002.Edge38,Board002.Edge38]
FEATURE [Assembly::JointGroup] Joints002
  Group = -> [GroundedJoint001,Joint002,Joint003,Joint004,Joint005,Joint006,Joint007,Joint008]
FEATURE [Assembly::AssemblyObject] Assembly002  label="M.2 HAT+ Assembly"
  Group = -> [Joints002,Board002,GroundedJoint001,Hole_Inserts,Hailo_Connector,Pin_Block,Hole_Inserts001,Hole_Inserts002,Hole_Inserts003,Joint002,Joint003,Joint004,Joint005,Joint006,Joint007,Joint008]
  Origin = -> Origin014
  Type = Assembly
FEATURE [App::Link] Board003  label="Board004"
  LinkedObject = -> Board002
FEATURE [App::Link] Hole_Inserts004  label="Hole Inserts005"
  LinkPlacement = pos=(-23.6422,-29.0551,0) rot=(0,0,1;0rad)
  LinkedObject = -> Hole_Inserts
  Placement = pos=(-23.6422,-29.0551,0) rot=(0,0,1;0rad)
FEATURE [App::Link] Hailo_Connector001  label="Hailo Connector002"
  LinkPlacement = pos=(-13.9,1.8e-15,1.57) rot=(0,0,1;0rad)
  LinkedObject = -> Hailo_Connector
  Placement = pos=(-13.9,1.8e-15,1.57) rot=(0,0,1;0rad)
FEATURE [App::Link] Pin_Block001  label="Pin Block002"
  LinkPlacement = pos=(1.6e-15,24.25,1.57) rot=(0,0,1;0rad)
  LinkedObject = -> Pin_Block
  Placement = pos=(1.6e-15,24.25,1.57) rot=(0,0,1;0rad)
FEATURE [App::Link] Hole_Inserts005  label="Hole Inserts006"
  LinkPlacement = pos=(34.3578,-29.0551,0) rot=(0,0,1;0rad)
  LinkedObject = -> Hole_Inserts001
  Placement = pos=(34.3578,-29.0551,0) rot=(0,0,1;0rad)
FEATURE [App::Link] Hole_Inserts006  label="Hole Inserts007"
  LinkPlacement = pos=(34.3578,20.4449,0) rot=(0,0,1;0rad)
  LinkedObject = -> Hole_Inserts002
  Placement = pos=(34.3578,20.4449,0) rot=(0,0,1;0rad)
FEATURE [App::Link] Hole_Inserts007  label="Hole Inserts008"
  LinkPlacement = pos=(-23.6422,20.4449,0) rot=(0,0,1;0rad)
  LinkedObject = -> Hole_Inserts003
  Placement = pos=(-23.6422,20.4449,0) rot=(0,0,1;0rad)
FEATURE [Assembly::AssemblyLink] M_2_HAT__Assembly  label="M.2 HAT+ Assembly001"
  Group = -> [Board003,Hole_Inserts004,Hailo_Connector001,Pin_Block001,Hole_Inserts005,Hole_Inserts006,Hole_Inserts007]
  LinkedObject = -> Assembly002
  Origin = -> Origin015
  Rigid = true
FEATURE [App::FeaturePython] GroundedJoint002  # Assembly grounded joint (typed FeaturePython)
  ObjectToGround = -> M_2_HAT__Assembly
FEATURE [App::Link] Board004  label="Board005"
  LinkedObject = -> Board
FEATURE [App::Link] Chip_Platform001  label="Chip Platform002"
  LinkPlacement = pos=(-2.02223,0.487867,0.8) rot=(0,0,1;0rad)
  LinkedObject = -> Chip_Platform
  Placement = pos=(-2.02223,0.487867,0.8) rot=(0,0,1;0rad)
FEATURE [App::Link] Chip001  label="Chip002"
  LinkPlacement = pos=(-2,1.8e-15,1.4) rot=(0,0,1;0rad)
  LinkedObject = -> Chip
  Placement = pos=(-2,1.8e-15,1.4) rot=(0,0,1;0rad)
FEATURE [Assembly::AssemblyLink] Hailo_AI_Module_Assembly  label="Hailo AI Module Assembly001"
  Group = -> [Board004,Chip_Platform001,Chip001]
  LinkedObject = -> Assembly
  Origin = -> Origin016
  Placement = pos=(7.45,2.4e-15,2.82) rot=(0,0,1;0rad)
  Rigid = true
FEATURE [App::FeaturePython] Joint009  label="Fixed009"  # Assembly joint (typed FeaturePython)
  Activated = true
  AngleMax = 0
  AngleMin = 0
  Detach1 = false
  Detach2 = false
  Distance = 0
  Distance2 = 0
  EnableAngleMax = false
  EnableAngleMin = false
  EnableLengthMax = false
  EnableLengthMin = false
  JointType = 0 (Fixed)
  LengthMax = 0
  LengthMin = 0
  Offset2 = pos=(0,-3.25,0) rot=(0,0,1;3.14159rad)
  Placement1 = pos=(-21,4e-15,0) rot=(-0.57735,-0.57735,0.57735;4.18879rad)
  Placement2 = pos=(0.35,0,1.25) rot=(0.57735,-0.57735,-0.57735;4.18879rad)
  Reference1 = -> Assembly001 [Hailo_AI_Module_Assembly.Board004.Edge21,Hailo_AI_Module_Assembly.Board004.Edge21]
  Reference2 = -> Assembly001 [M_2_HAT__Assembly.Hailo_Connector001.Edge7,M_2_HAT__Assembly.Hailo_Connector001.Edge7]
FEATURE [App::Link] Pin  label="Pin001"
  LinkPlacement = pos=(28.45,2.4e-15,-2.1439) rot=(0,0,1;3.14159rad)
  LinkedObject = -> Body001
  Placement = pos=(28.45,2.4e-15,-2.1439) rot=(0,0,1;3.14159rad)
FEATURE [App::FeaturePython] Joint010  label="Fixed010"  # Assembly joint (typed FeaturePython)
  Activated = true
  AngleMax = 0
  AngleMin = 0
  Detach1 = false
  Detach2 = false
  Distance = 0
  Distance2 = 0
  EnableAngleMax = false
  EnableAngleMin = false
  EnableLengthMax = false
  EnableLengthMin = false
  JointType = 0 (Fixed)
  LengthMax = 0
  LengthMin = 0
  Placement1 = pos=(0,0,5.7639) rot=(0,0,-1;3.14159rad)
  Placement2 = pos=(21,0,0.8) rot=(0,0,1;0rad)
  Reference1 = -> Assembly001 [Pin.Edge8,Pin.Edge8]
  Reference2 = -> Assembly001 [Hailo_AI_Module_Assembly.Board004.Edge35,Hailo_AI_Module_Assembly.Board004.Edge35]
FEATURE [Assembly::JointGroup] Joints001
  Group = -> [GroundedJoint002,Joint009,Joint010]
FEATURE [Assembly::AssemblyObject] Assembly001  label="Raspberry Pi AI Kit"
  Group = -> [Joints001,M_2_HAT__Assembly,GroundedJoint002,Hailo_AI_Module_Assembly,Joint009,Pin,Joint010]
  Origin = -> Origin009
  Type = Assembly
